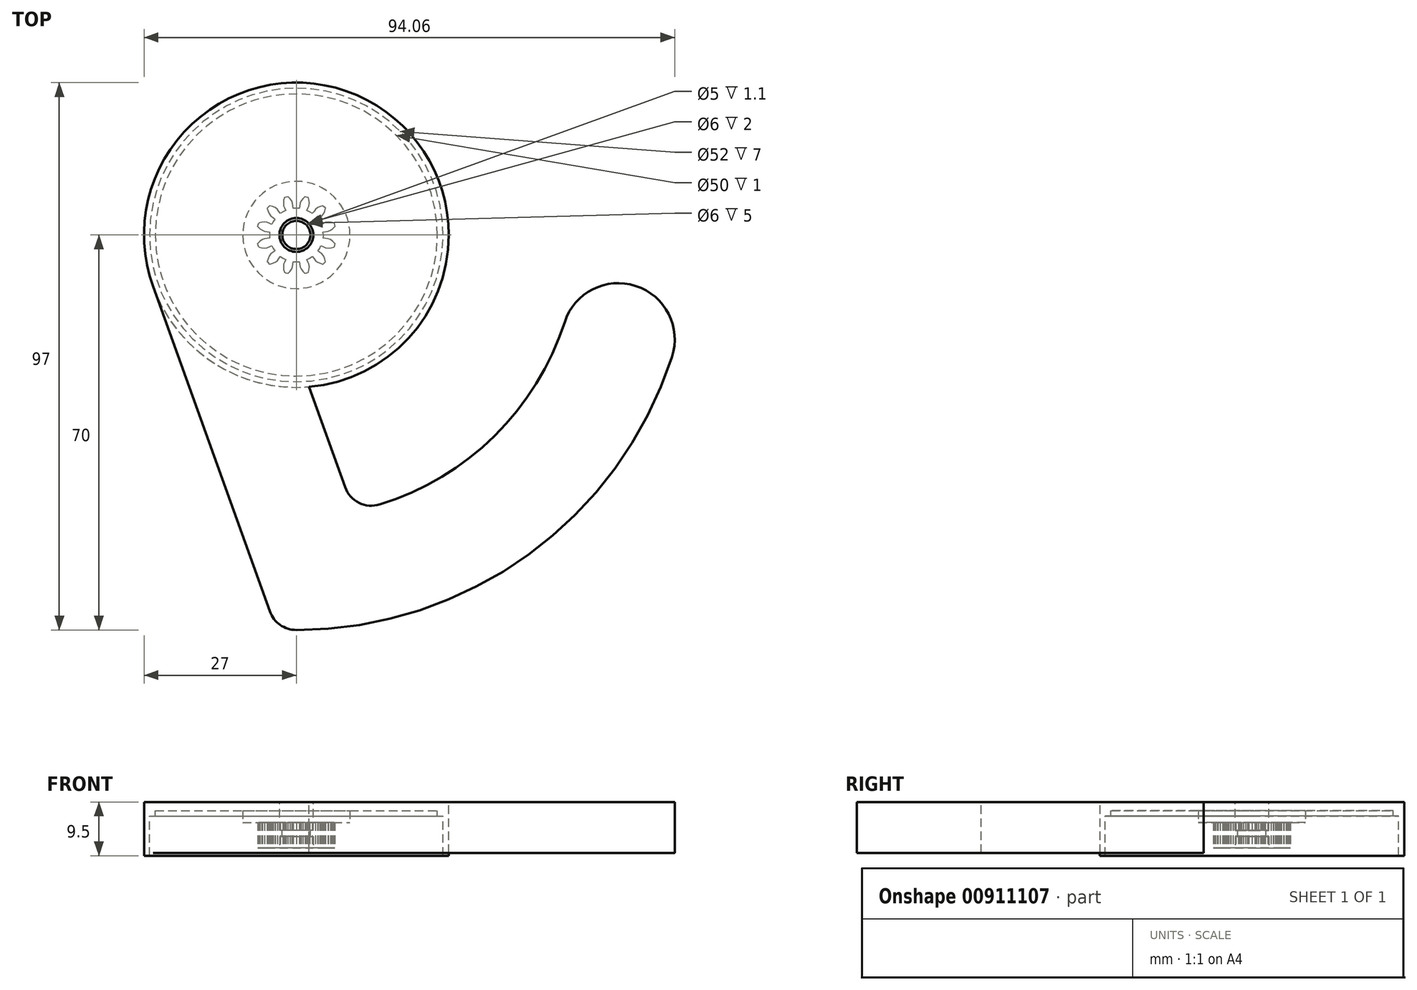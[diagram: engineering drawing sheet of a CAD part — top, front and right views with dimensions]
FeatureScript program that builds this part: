
annotation { "Feature Type Name" : "Feature", "Feature Type Description" : "" }
export const myFeature = defineFeature(function(context is Context, id is Id, definition is map)
    precondition{}
    {
        {
            var Q0;
            Q0=qCreatedBy(makeId("Top.planeOp"),FACE);
            var sketch = newSketch(context, id + "F0", { "sketchPlane" : qUnion([Q0])});
            skLineSegment(sketch, "E0", {"start": v(4.75, 0) * mm, "end": v(4.72, 0.55) * mm});
            skLineSegment(sketch, "E1", {"start": v(4.72, 0.55) * mm, "end": v(5.17, 0.6) * mm});
            skLineSegment(sketch, "E2", {"start": v(5.17, 0.6) * mm, "end": v(5.61, 0.65) * mm});
            skLineSegment(sketch, "E3", {"start": v(5.61, 0.65) * mm, "end": v(6.04, 0.84) * mm});
            skLineSegment(sketch, "E4", {"start": v(6.04, 0.84) * mm, "end": v(6.45, 1.13) * mm});
            skLineSegment(sketch, "E5", {"start": v(6.45, 1.13) * mm, "end": v(6.84, 1.51) * mm});
            skLineSegment(sketch, "E6", {"start": v(6.84, 1.51) * mm, "end": v(6.76, 1.81) * mm});
            skLineSegment(sketch, "E7", {"start": v(6.76, 1.81) * mm, "end": v(6.67, 2.1) * mm});
            skLineSegment(sketch, "E8", {"start": v(6.67, 2.1) * mm, "end": v(6.15, 2.25) * mm});
            skLineSegment(sketch, "E9", {"start": v(6.15, 2.25) * mm, "end": v(5.65, 2.3) * mm});
            skLineSegment(sketch, "E10", {"start": v(5.65, 2.3) * mm, "end": v(5.19, 2.24) * mm});
            skLineSegment(sketch, "E11", {"start": v(5.19, 2.24) * mm, "end": v(4.77, 2.06) * mm});
            skLineSegment(sketch, "E12", {"start": v(4.77, 2.06) * mm, "end": v(4.36, 1.88) * mm});
            skLineSegment(sketch, "E13", {"start": v(4.36, 1.88) * mm, "end": v(4.11, 2.38) * mm});
            skLineSegment(sketch, "E14", {"start": v(4.11, 2.38) * mm, "end": v(3.81, 2.84) * mm});
            skLineSegment(sketch, "E15", {"start": v(3.81, 2.84) * mm, "end": v(4.17, 3.1) * mm});
            skLineSegment(sketch, "E16", {"start": v(4.17, 3.1) * mm, "end": v(4.53, 3.37) * mm});
            skLineSegment(sketch, "E17", {"start": v(4.53, 3.37) * mm, "end": v(4.82, 3.74) * mm});
            skLineSegment(sketch, "E18", {"start": v(4.82, 3.74) * mm, "end": v(5.02, 4.2) * mm});
            skLineSegment(sketch, "E19", {"start": v(5.02, 4.2) * mm, "end": v(5.16, 4.73) * mm});
            skLineSegment(sketch, "E20", {"start": v(5.16, 4.73) * mm, "end": v(4.95, 4.95) * mm});
            skLineSegment(sketch, "E21", {"start": v(4.95, 4.95) * mm, "end": v(4.73, 5.16) * mm});
            skLineSegment(sketch, "E22", {"start": v(4.73, 5.16) * mm, "end": v(4.2, 5.02) * mm});
            skLineSegment(sketch, "E23", {"start": v(4.2, 5.02) * mm, "end": v(3.74, 4.82) * mm});
            skLineSegment(sketch, "E24", {"start": v(3.74, 4.82) * mm, "end": v(3.37, 4.53) * mm});
            skLineSegment(sketch, "E25", {"start": v(3.37, 4.53) * mm, "end": v(3.1, 4.17) * mm});
            skLineSegment(sketch, "E26", {"start": v(3.1, 4.17) * mm, "end": v(2.84, 3.81) * mm});
            skLineSegment(sketch, "E27", {"start": v(2.84, 3.81) * mm, "end": v(2.38, 4.11) * mm});
            skLineSegment(sketch, "E28", {"start": v(2.38, 4.11) * mm, "end": v(1.88, 4.36) * mm});
            skLineSegment(sketch, "E29", {"start": v(1.88, 4.36) * mm, "end": v(2.06, 4.77) * mm});
            skLineSegment(sketch, "E30", {"start": v(2.06, 4.77) * mm, "end": v(2.24, 5.19) * mm});
            skLineSegment(sketch, "E31", {"start": v(2.24, 5.19) * mm, "end": v(2.3, 5.65) * mm});
            skLineSegment(sketch, "E32", {"start": v(2.3, 5.65) * mm, "end": v(2.25, 6.15) * mm});
            skLineSegment(sketch, "E33", {"start": v(2.25, 6.15) * mm, "end": v(2.1, 6.67) * mm});
            skLineSegment(sketch, "E34", {"start": v(2.1, 6.67) * mm, "end": v(1.81, 6.76) * mm});
            skLineSegment(sketch, "E35", {"start": v(1.81, 6.76) * mm, "end": v(1.51, 6.84) * mm});
            skLineSegment(sketch, "E36", {"start": v(1.51, 6.84) * mm, "end": v(1.13, 6.45) * mm});
            skLineSegment(sketch, "E37", {"start": v(1.13, 6.45) * mm, "end": v(0.84, 6.04) * mm});
            skLineSegment(sketch, "E38", {"start": v(0.84, 6.04) * mm, "end": v(0.65, 5.61) * mm});
            skLineSegment(sketch, "E39", {"start": v(0.65, 5.61) * mm, "end": v(0.6, 5.17) * mm});
            skLineSegment(sketch, "E40", {"start": v(0.6, 5.17) * mm, "end": v(0.55, 4.72) * mm});
            skLineSegment(sketch, "E41", {"start": v(0.55, 4.72) * mm, "end": v(0, 4.75) * mm});
            skLineSegment(sketch, "E42", {"start": v(0, 4.75) * mm, "end": v(-0.55, 4.72) * mm});
            skLineSegment(sketch, "E43", {"start": v(-0.55, 4.72) * mm, "end": v(-0.6, 5.17) * mm});
            skLineSegment(sketch, "E44", {"start": v(-0.6, 5.17) * mm, "end": v(-0.65, 5.61) * mm});
            skLineSegment(sketch, "E45", {"start": v(-0.65, 5.61) * mm, "end": v(-0.84, 6.04) * mm});
            skLineSegment(sketch, "E46", {"start": v(-0.84, 6.04) * mm, "end": v(-1.13, 6.45) * mm});
            skLineSegment(sketch, "E47", {"start": v(-1.13, 6.45) * mm, "end": v(-1.51, 6.84) * mm});
            skLineSegment(sketch, "E48", {"start": v(-1.51, 6.84) * mm, "end": v(-1.81, 6.76) * mm});
            skLineSegment(sketch, "E49", {"start": v(-1.81, 6.76) * mm, "end": v(-2.1, 6.67) * mm});
            skLineSegment(sketch, "E50", {"start": v(-2.1, 6.67) * mm, "end": v(-2.25, 6.15) * mm});
            skLineSegment(sketch, "E51", {"start": v(-2.25, 6.15) * mm, "end": v(-2.3, 5.65) * mm});
            skLineSegment(sketch, "E52", {"start": v(-2.3, 5.65) * mm, "end": v(-2.24, 5.19) * mm});
            skLineSegment(sketch, "E53", {"start": v(-2.24, 5.19) * mm, "end": v(-2.06, 4.77) * mm});
            skLineSegment(sketch, "E54", {"start": v(-2.06, 4.77) * mm, "end": v(-1.88, 4.36) * mm});
            skLineSegment(sketch, "E55", {"start": v(-1.88, 4.36) * mm, "end": v(-2.38, 4.11) * mm});
            skLineSegment(sketch, "E56", {"start": v(-2.38, 4.11) * mm, "end": v(-2.84, 3.81) * mm});
            skLineSegment(sketch, "E57", {"start": v(-2.84, 3.81) * mm, "end": v(-3.1, 4.17) * mm});
            skLineSegment(sketch, "E58", {"start": v(-3.1, 4.17) * mm, "end": v(-3.37, 4.53) * mm});
            skLineSegment(sketch, "E59", {"start": v(-3.37, 4.53) * mm, "end": v(-3.74, 4.82) * mm});
            skLineSegment(sketch, "E60", {"start": v(-3.74, 4.82) * mm, "end": v(-4.2, 5.02) * mm});
            skLineSegment(sketch, "E61", {"start": v(-4.2, 5.02) * mm, "end": v(-4.73, 5.16) * mm});
            skLineSegment(sketch, "E62", {"start": v(-4.73, 5.16) * mm, "end": v(-4.95, 4.95) * mm});
            skLineSegment(sketch, "E63", {"start": v(-4.95, 4.95) * mm, "end": v(-5.16, 4.73) * mm});
            skLineSegment(sketch, "E64", {"start": v(-5.16, 4.73) * mm, "end": v(-5.02, 4.2) * mm});
            skLineSegment(sketch, "E65", {"start": v(-5.02, 4.2) * mm, "end": v(-4.82, 3.74) * mm});
            skLineSegment(sketch, "E66", {"start": v(-4.82, 3.74) * mm, "end": v(-4.53, 3.37) * mm});
            skLineSegment(sketch, "E67", {"start": v(-4.53, 3.37) * mm, "end": v(-4.17, 3.1) * mm});
            skLineSegment(sketch, "E68", {"start": v(-4.17, 3.1) * mm, "end": v(-3.81, 2.84) * mm});
            skLineSegment(sketch, "E69", {"start": v(-3.81, 2.84) * mm, "end": v(-4.11, 2.38) * mm});
            skLineSegment(sketch, "E70", {"start": v(-4.11, 2.38) * mm, "end": v(-4.36, 1.88) * mm});
            skLineSegment(sketch, "E71", {"start": v(-4.36, 1.88) * mm, "end": v(-4.77, 2.06) * mm});
            skLineSegment(sketch, "E72", {"start": v(-4.77, 2.06) * mm, "end": v(-5.19, 2.24) * mm});
            skLineSegment(sketch, "E73", {"start": v(-5.19, 2.24) * mm, "end": v(-5.65, 2.3) * mm});
            skLineSegment(sketch, "E74", {"start": v(-5.65, 2.3) * mm, "end": v(-6.15, 2.25) * mm});
            skLineSegment(sketch, "E75", {"start": v(-6.15, 2.25) * mm, "end": v(-6.67, 2.1) * mm});
            skLineSegment(sketch, "E76", {"start": v(-6.67, 2.1) * mm, "end": v(-6.76, 1.81) * mm});
            skLineSegment(sketch, "E77", {"start": v(-6.76, 1.81) * mm, "end": v(-6.84, 1.51) * mm});
            skLineSegment(sketch, "E78", {"start": v(-6.84, 1.51) * mm, "end": v(-6.45, 1.13) * mm});
            skLineSegment(sketch, "E79", {"start": v(-6.45, 1.13) * mm, "end": v(-6.04, 0.84) * mm});
            skLineSegment(sketch, "E80", {"start": v(-6.04, 0.84) * mm, "end": v(-5.61, 0.65) * mm});
            skLineSegment(sketch, "E81", {"start": v(-5.61, 0.65) * mm, "end": v(-5.17, 0.6) * mm});
            skLineSegment(sketch, "E82", {"start": v(-5.17, 0.6) * mm, "end": v(-4.72, 0.55) * mm});
            skLineSegment(sketch, "E83", {"start": v(-4.72, 0.55) * mm, "end": v(-4.75, 0) * mm});
            skLineSegment(sketch, "E84", {"start": v(-4.75, 0) * mm, "end": v(-4.72, -0.55) * mm});
            skLineSegment(sketch, "E85", {"start": v(-4.72, -0.55) * mm, "end": v(-5.17, -0.6) * mm});
            skLineSegment(sketch, "E86", {"start": v(-5.17, -0.6) * mm, "end": v(-5.61, -0.65) * mm});
            skLineSegment(sketch, "E87", {"start": v(-5.61, -0.65) * mm, "end": v(-6.04, -0.84) * mm});
            skLineSegment(sketch, "E88", {"start": v(-6.04, -0.84) * mm, "end": v(-6.45, -1.13) * mm});
            skLineSegment(sketch, "E89", {"start": v(-6.45, -1.13) * mm, "end": v(-6.84, -1.51) * mm});
            skLineSegment(sketch, "E90", {"start": v(-6.84, -1.51) * mm, "end": v(-6.76, -1.81) * mm});
            skLineSegment(sketch, "E91", {"start": v(-6.76, -1.81) * mm, "end": v(-6.67, -2.1) * mm});
            skLineSegment(sketch, "E92", {"start": v(-6.67, -2.1) * mm, "end": v(-6.15, -2.25) * mm});
            skLineSegment(sketch, "E93", {"start": v(-6.15, -2.25) * mm, "end": v(-5.65, -2.3) * mm});
            skLineSegment(sketch, "E94", {"start": v(-5.65, -2.3) * mm, "end": v(-5.19, -2.24) * mm});
            skLineSegment(sketch, "E95", {"start": v(-5.19, -2.24) * mm, "end": v(-4.77, -2.06) * mm});
            skLineSegment(sketch, "E96", {"start": v(-4.77, -2.06) * mm, "end": v(-4.36, -1.88) * mm});
            skLineSegment(sketch, "E97", {"start": v(-4.36, -1.88) * mm, "end": v(-4.11, -2.38) * mm});
            skLineSegment(sketch, "E98", {"start": v(-4.11, -2.38) * mm, "end": v(-3.81, -2.84) * mm});
            skLineSegment(sketch, "E99", {"start": v(-3.81, -2.84) * mm, "end": v(-4.17, -3.1) * mm});
            skLineSegment(sketch, "E100", {"start": v(-4.17, -3.1) * mm, "end": v(-4.53, -3.37) * mm});
            skLineSegment(sketch, "E101", {"start": v(-4.53, -3.37) * mm, "end": v(-4.82, -3.74) * mm});
            skLineSegment(sketch, "E102", {"start": v(-4.82, -3.74) * mm, "end": v(-5.02, -4.2) * mm});
            skLineSegment(sketch, "E103", {"start": v(-5.02, -4.2) * mm, "end": v(-5.16, -4.73) * mm});
            skLineSegment(sketch, "E104", {"start": v(-5.16, -4.73) * mm, "end": v(-4.95, -4.95) * mm});
            skLineSegment(sketch, "E105", {"start": v(-4.95, -4.95) * mm, "end": v(-4.73, -5.16) * mm});
            skLineSegment(sketch, "E106", {"start": v(-4.73, -5.16) * mm, "end": v(-4.2, -5.02) * mm});
            skLineSegment(sketch, "E107", {"start": v(-4.2, -5.02) * mm, "end": v(-3.74, -4.82) * mm});
            skLineSegment(sketch, "E108", {"start": v(-3.74, -4.82) * mm, "end": v(-3.37, -4.53) * mm});
            skLineSegment(sketch, "E109", {"start": v(-3.37, -4.53) * mm, "end": v(-3.1, -4.17) * mm});
            skLineSegment(sketch, "E110", {"start": v(-3.1, -4.17) * mm, "end": v(-2.84, -3.81) * mm});
            skLineSegment(sketch, "E111", {"start": v(-2.84, -3.81) * mm, "end": v(-2.38, -4.11) * mm});
            skLineSegment(sketch, "E112", {"start": v(-2.38, -4.11) * mm, "end": v(-1.88, -4.36) * mm});
            skLineSegment(sketch, "E113", {"start": v(-1.88, -4.36) * mm, "end": v(-2.06, -4.77) * mm});
            skLineSegment(sketch, "E114", {"start": v(-2.06, -4.77) * mm, "end": v(-2.24, -5.19) * mm});
            skLineSegment(sketch, "E115", {"start": v(-2.24, -5.19) * mm, "end": v(-2.3, -5.65) * mm});
            skLineSegment(sketch, "E116", {"start": v(-2.3, -5.65) * mm, "end": v(-2.25, -6.15) * mm});
            skLineSegment(sketch, "E117", {"start": v(-2.25, -6.15) * mm, "end": v(-2.1, -6.67) * mm});
            skLineSegment(sketch, "E118", {"start": v(-2.1, -6.67) * mm, "end": v(-1.81, -6.76) * mm});
            skLineSegment(sketch, "E119", {"start": v(-1.81, -6.76) * mm, "end": v(-1.51, -6.84) * mm});
            skLineSegment(sketch, "E120", {"start": v(-1.51, -6.84) * mm, "end": v(-1.13, -6.45) * mm});
            skLineSegment(sketch, "E121", {"start": v(-1.13, -6.45) * mm, "end": v(-0.84, -6.04) * mm});
            skLineSegment(sketch, "E122", {"start": v(-0.84, -6.04) * mm, "end": v(-0.65, -5.61) * mm});
            skLineSegment(sketch, "E123", {"start": v(-0.65, -5.61) * mm, "end": v(-0.6, -5.17) * mm});
            skLineSegment(sketch, "E124", {"start": v(-0.6, -5.17) * mm, "end": v(-0.55, -4.72) * mm});
            skLineSegment(sketch, "E125", {"start": v(-0.55, -4.72) * mm, "end": v(0, -4.75) * mm});
            skLineSegment(sketch, "E126", {"start": v(0, -4.75) * mm, "end": v(0.55, -4.72) * mm});
            skLineSegment(sketch, "E127", {"start": v(0.55, -4.72) * mm, "end": v(0.6, -5.17) * mm});
            skLineSegment(sketch, "E128", {"start": v(0.6, -5.17) * mm, "end": v(0.65, -5.61) * mm});
            skLineSegment(sketch, "E129", {"start": v(0.65, -5.61) * mm, "end": v(0.84, -6.04) * mm});
            skLineSegment(sketch, "E130", {"start": v(0.84, -6.04) * mm, "end": v(1.13, -6.45) * mm});
            skLineSegment(sketch, "E131", {"start": v(1.13, -6.45) * mm, "end": v(1.51, -6.84) * mm});
            skLineSegment(sketch, "E132", {"start": v(1.51, -6.84) * mm, "end": v(1.81, -6.76) * mm});
            skLineSegment(sketch, "E133", {"start": v(1.81, -6.76) * mm, "end": v(2.1, -6.67) * mm});
            skLineSegment(sketch, "E134", {"start": v(2.1, -6.67) * mm, "end": v(2.25, -6.15) * mm});
            skLineSegment(sketch, "E135", {"start": v(2.25, -6.15) * mm, "end": v(2.3, -5.65) * mm});
            skLineSegment(sketch, "E136", {"start": v(2.3, -5.65) * mm, "end": v(2.24, -5.19) * mm});
            skLineSegment(sketch, "E137", {"start": v(2.24, -5.19) * mm, "end": v(2.06, -4.77) * mm});
            skLineSegment(sketch, "E138", {"start": v(2.06, -4.77) * mm, "end": v(1.88, -4.36) * mm});
            skLineSegment(sketch, "E139", {"start": v(1.88, -4.36) * mm, "end": v(2.38, -4.11) * mm});
            skLineSegment(sketch, "E140", {"start": v(2.38, -4.11) * mm, "end": v(2.84, -3.81) * mm});
            skLineSegment(sketch, "E141", {"start": v(2.84, -3.81) * mm, "end": v(3.1, -4.17) * mm});
            skLineSegment(sketch, "E142", {"start": v(3.1, -4.17) * mm, "end": v(3.37, -4.53) * mm});
            skLineSegment(sketch, "E143", {"start": v(3.37, -4.53) * mm, "end": v(3.74, -4.82) * mm});
            skLineSegment(sketch, "E144", {"start": v(3.74, -4.82) * mm, "end": v(4.2, -5.02) * mm});
            skLineSegment(sketch, "E145", {"start": v(4.2, -5.02) * mm, "end": v(4.73, -5.16) * mm});
            skLineSegment(sketch, "E146", {"start": v(4.73, -5.16) * mm, "end": v(4.95, -4.95) * mm});
            skLineSegment(sketch, "E147", {"start": v(4.95, -4.95) * mm, "end": v(5.16, -4.73) * mm});
            skLineSegment(sketch, "E148", {"start": v(5.16, -4.73) * mm, "end": v(5.02, -4.2) * mm});
            skLineSegment(sketch, "E149", {"start": v(5.02, -4.2) * mm, "end": v(4.82, -3.74) * mm});
            skLineSegment(sketch, "E150", {"start": v(4.82, -3.74) * mm, "end": v(4.53, -3.37) * mm});
            skLineSegment(sketch, "E151", {"start": v(4.53, -3.37) * mm, "end": v(4.17, -3.1) * mm});
            skLineSegment(sketch, "E152", {"start": v(4.17, -3.1) * mm, "end": v(3.81, -2.84) * mm});
            skLineSegment(sketch, "E153", {"start": v(3.81, -2.84) * mm, "end": v(4.11, -2.38) * mm});
            skLineSegment(sketch, "E154", {"start": v(4.11, -2.38) * mm, "end": v(4.36, -1.88) * mm});
            skLineSegment(sketch, "E155", {"start": v(4.36, -1.88) * mm, "end": v(4.77, -2.06) * mm});
            skLineSegment(sketch, "E156", {"start": v(4.77, -2.06) * mm, "end": v(5.19, -2.24) * mm});
            skLineSegment(sketch, "E157", {"start": v(5.19, -2.24) * mm, "end": v(5.65, -2.3) * mm});
            skLineSegment(sketch, "E158", {"start": v(5.65, -2.3) * mm, "end": v(6.15, -2.25) * mm});
            skLineSegment(sketch, "E159", {"start": v(6.15, -2.25) * mm, "end": v(6.67, -2.1) * mm});
            skLineSegment(sketch, "E160", {"start": v(6.67, -2.1) * mm, "end": v(6.76, -1.81) * mm});
            skLineSegment(sketch, "E161", {"start": v(6.76, -1.81) * mm, "end": v(6.84, -1.51) * mm});
            skLineSegment(sketch, "E162", {"start": v(6.84, -1.51) * mm, "end": v(6.45, -1.13) * mm});
            skLineSegment(sketch, "E163", {"start": v(6.45, -1.13) * mm, "end": v(6.04, -0.84) * mm});
            skLineSegment(sketch, "E164", {"start": v(6.04, -0.84) * mm, "end": v(5.61, -0.65) * mm});
            skLineSegment(sketch, "E165", {"start": v(5.61, -0.65) * mm, "end": v(5.17, -0.6) * mm});
            skLineSegment(sketch, "E166", {"start": v(5.17, -0.6) * mm, "end": v(4.72, -0.55) * mm});
            skLineSegment(sketch, "E167", {"start": v(4.75, 0) * mm, "end": v(4.72, -0.55) * mm});
            skSolve(sketch);
        }
        {
            var Q0;
            Q0 = qSketchRegion(id + "F0", true);
            extrude(context, id + "F1", {"entities" : qUnion([Q0]), "depth" : 6 * mm, "offsetDistance" : 25 * mm});
        }
        {
            var Q0;
            Q0=makeQuery(id+"F1.opExtrude","CAP_FACE",FACE,{"disambiguationData":[OSD([sQuery(id+"F0.wireOp",EDGE,"E0"),sQuery(id+"F0.wireOp",EDGE,"E1"),sQuery(id+"F0.wireOp",EDGE,"E2"),sQuery(id+"F0.wireOp",EDGE,"E3"),sQuery(id+"F0.wireOp",EDGE,"E4"),sQuery(id+"F0.wireOp",EDGE,"E5"),sQuery(id+"F0.wireOp",EDGE,"E6"),sQuery(id+"F0.wireOp",EDGE,"E7"),sQuery(id+"F0.wireOp",EDGE,"E8"),sQuery(id+"F0.wireOp",EDGE,"E9"),sQuery(id+"F0.wireOp",EDGE,"E10"),sQuery(id+"F0.wireOp",EDGE,"E11"),sQuery(id+"F0.wireOp",EDGE,"E12"),sQuery(id+"F0.wireOp",EDGE,"E13"),sQuery(id+"F0.wireOp",EDGE,"E14"),sQuery(id+"F0.wireOp",EDGE,"E15"),sQuery(id+"F0.wireOp",EDGE,"E16"),sQuery(id+"F0.wireOp",EDGE,"E17"),sQuery(id+"F0.wireOp",EDGE,"E18"),sQuery(id+"F0.wireOp",EDGE,"E19"),sQuery(id+"F0.wireOp",EDGE,"E20"),sQuery(id+"F0.wireOp",EDGE,"E21"),sQuery(id+"F0.wireOp",EDGE,"E22"),sQuery(id+"F0.wireOp",EDGE,"E23"),sQuery(id+"F0.wireOp",EDGE,"E24"),sQuery(id+"F0.wireOp",EDGE,"E25"),sQuery(id+"F0.wireOp",EDGE,"E26"),sQuery(id+"F0.wireOp",EDGE,"E27"),sQuery(id+"F0.wireOp",EDGE,"E28"),sQuery(id+"F0.wireOp",EDGE,"E29"),sQuery(id+"F0.wireOp",EDGE,"E30"),sQuery(id+"F0.wireOp",EDGE,"E31"),sQuery(id+"F0.wireOp",EDGE,"E32"),sQuery(id+"F0.wireOp",EDGE,"E33"),sQuery(id+"F0.wireOp",EDGE,"E34"),sQuery(id+"F0.wireOp",EDGE,"E35"),sQuery(id+"F0.wireOp",EDGE,"E36"),sQuery(id+"F0.wireOp",EDGE,"E37"),sQuery(id+"F0.wireOp",EDGE,"E38"),sQuery(id+"F0.wireOp",EDGE,"E39"),sQuery(id+"F0.wireOp",EDGE,"E40"),sQuery(id+"F0.wireOp",EDGE,"E41"),sQuery(id+"F0.wireOp",EDGE,"E42"),sQuery(id+"F0.wireOp",EDGE,"E43"),sQuery(id+"F0.wireOp",EDGE,"E44"),sQuery(id+"F0.wireOp",EDGE,"E45"),sQuery(id+"F0.wireOp",EDGE,"E46"),sQuery(id+"F0.wireOp",EDGE,"E47"),sQuery(id+"F0.wireOp",EDGE,"E48"),sQuery(id+"F0.wireOp",EDGE,"E49"),sQuery(id+"F0.wireOp",EDGE,"E50"),sQuery(id+"F0.wireOp",EDGE,"E51"),sQuery(id+"F0.wireOp",EDGE,"E52"),sQuery(id+"F0.wireOp",EDGE,"E53"),sQuery(id+"F0.wireOp",EDGE,"E54"),sQuery(id+"F0.wireOp",EDGE,"E55"),sQuery(id+"F0.wireOp",EDGE,"E56"),sQuery(id+"F0.wireOp",EDGE,"E57"),sQuery(id+"F0.wireOp",EDGE,"E58"),sQuery(id+"F0.wireOp",EDGE,"E59"),sQuery(id+"F0.wireOp",EDGE,"E60"),sQuery(id+"F0.wireOp",EDGE,"E61"),sQuery(id+"F0.wireOp",EDGE,"E62"),sQuery(id+"F0.wireOp",EDGE,"E63"),sQuery(id+"F0.wireOp",EDGE,"E64"),sQuery(id+"F0.wireOp",EDGE,"E65"),sQuery(id+"F0.wireOp",EDGE,"E66"),sQuery(id+"F0.wireOp",EDGE,"E67"),sQuery(id+"F0.wireOp",EDGE,"E68"),sQuery(id+"F0.wireOp",EDGE,"E69"),sQuery(id+"F0.wireOp",EDGE,"E70"),sQuery(id+"F0.wireOp",EDGE,"E71"),sQuery(id+"F0.wireOp",EDGE,"E72"),sQuery(id+"F0.wireOp",EDGE,"E73"),sQuery(id+"F0.wireOp",EDGE,"E74"),sQuery(id+"F0.wireOp",EDGE,"E75"),sQuery(id+"F0.wireOp",EDGE,"E76"),sQuery(id+"F0.wireOp",EDGE,"E77"),sQuery(id+"F0.wireOp",EDGE,"E78"),sQuery(id+"F0.wireOp",EDGE,"E79"),sQuery(id+"F0.wireOp",EDGE,"E80"),sQuery(id+"F0.wireOp",EDGE,"E81"),sQuery(id+"F0.wireOp",EDGE,"E82"),sQuery(id+"F0.wireOp",EDGE,"E83"),sQuery(id+"F0.wireOp",EDGE,"E84"),sQuery(id+"F0.wireOp",EDGE,"E85"),sQuery(id+"F0.wireOp",EDGE,"E86"),sQuery(id+"F0.wireOp",EDGE,"E87"),sQuery(id+"F0.wireOp",EDGE,"E88"),sQuery(id+"F0.wireOp",EDGE,"E89"),sQuery(id+"F0.wireOp",EDGE,"E90"),sQuery(id+"F0.wireOp",EDGE,"E91"),sQuery(id+"F0.wireOp",EDGE,"E92"),sQuery(id+"F0.wireOp",EDGE,"E93"),sQuery(id+"F0.wireOp",EDGE,"E94"),sQuery(id+"F0.wireOp",EDGE,"E95"),sQuery(id+"F0.wireOp",EDGE,"E96"),sQuery(id+"F0.wireOp",EDGE,"E97"),sQuery(id+"F0.wireOp",EDGE,"E98"),sQuery(id+"F0.wireOp",EDGE,"E99"),sQuery(id+"F0.wireOp",EDGE,"E100"),sQuery(id+"F0.wireOp",EDGE,"E101"),sQuery(id+"F0.wireOp",EDGE,"E102"),sQuery(id+"F0.wireOp",EDGE,"E103"),sQuery(id+"F0.wireOp",EDGE,"E104"),sQuery(id+"F0.wireOp",EDGE,"E105"),sQuery(id+"F0.wireOp",EDGE,"E106"),sQuery(id+"F0.wireOp",EDGE,"E107"),sQuery(id+"F0.wireOp",EDGE,"E108"),sQuery(id+"F0.wireOp",EDGE,"E109"),sQuery(id+"F0.wireOp",EDGE,"E110"),sQuery(id+"F0.wireOp",EDGE,"E111"),sQuery(id+"F0.wireOp",EDGE,"E112"),sQuery(id+"F0.wireOp",EDGE,"E113"),sQuery(id+"F0.wireOp",EDGE,"E114"),sQuery(id+"F0.wireOp",EDGE,"E115"),sQuery(id+"F0.wireOp",EDGE,"E116"),sQuery(id+"F0.wireOp",EDGE,"E117"),sQuery(id+"F0.wireOp",EDGE,"E118"),sQuery(id+"F0.wireOp",EDGE,"E119"),sQuery(id+"F0.wireOp",EDGE,"E120"),sQuery(id+"F0.wireOp",EDGE,"E121"),sQuery(id+"F0.wireOp",EDGE,"E122"),sQuery(id+"F0.wireOp",EDGE,"E123"),sQuery(id+"F0.wireOp",EDGE,"E124"),sQuery(id+"F0.wireOp",EDGE,"E125"),sQuery(id+"F0.wireOp",EDGE,"E126"),sQuery(id+"F0.wireOp",EDGE,"E127"),sQuery(id+"F0.wireOp",EDGE,"E128"),sQuery(id+"F0.wireOp",EDGE,"E129"),sQuery(id+"F0.wireOp",EDGE,"E130"),sQuery(id+"F0.wireOp",EDGE,"E131"),sQuery(id+"F0.wireOp",EDGE,"E132"),sQuery(id+"F0.wireOp",EDGE,"E133"),sQuery(id+"F0.wireOp",EDGE,"E134"),sQuery(id+"F0.wireOp",EDGE,"E135"),sQuery(id+"F0.wireOp",EDGE,"E136"),sQuery(id+"F0.wireOp",EDGE,"E137"),sQuery(id+"F0.wireOp",EDGE,"E138"),sQuery(id+"F0.wireOp",EDGE,"E139"),sQuery(id+"F0.wireOp",EDGE,"E140"),sQuery(id+"F0.wireOp",EDGE,"E141"),sQuery(id+"F0.wireOp",EDGE,"E142"),sQuery(id+"F0.wireOp",EDGE,"E143"),sQuery(id+"F0.wireOp",EDGE,"E144"),sQuery(id+"F0.wireOp",EDGE,"E145"),sQuery(id+"F0.wireOp",EDGE,"E146"),sQuery(id+"F0.wireOp",EDGE,"E147"),sQuery(id+"F0.wireOp",EDGE,"E148"),sQuery(id+"F0.wireOp",EDGE,"E149"),sQuery(id+"F0.wireOp",EDGE,"E150"),sQuery(id+"F0.wireOp",EDGE,"E151"),sQuery(id+"F0.wireOp",EDGE,"E152"),sQuery(id+"F0.wireOp",EDGE,"E153"),sQuery(id+"F0.wireOp",EDGE,"E154"),sQuery(id+"F0.wireOp",EDGE,"E155"),sQuery(id+"F0.wireOp",EDGE,"E156"),sQuery(id+"F0.wireOp",EDGE,"E157"),sQuery(id+"F0.wireOp",EDGE,"E158"),sQuery(id+"F0.wireOp",EDGE,"E159"),sQuery(id+"F0.wireOp",EDGE,"E160"),sQuery(id+"F0.wireOp",EDGE,"E161"),sQuery(id+"F0.wireOp",EDGE,"E162"),sQuery(id+"F0.wireOp",EDGE,"E163"),sQuery(id+"F0.wireOp",EDGE,"E164"),sQuery(id+"F0.wireOp",EDGE,"E165"),sQuery(id+"F0.wireOp",EDGE,"E166"),sQuery(id+"F0.wireOp",EDGE,"E167")])],"isStart":true});
            var sketch = newSketch(context, id + "F2", { "sketchPlane" : qUnion([Q0])});
            skCircle(sketch, "E168", {"center": v(0, 0) * mm, "radius": 3 * mm});
            skSolve(sketch);
        }
        {
            var Q0;
            Q0 = qSketchRegion(id + "F2", true);
            extrude(context, id + "F3", {"entities" : qUnion([Q0]), "operationType" : NewBodyOperationType.REMOVE, "oppositeDirection" : true, "depth" : 2 * mm, "offsetDistance" : 25 * mm});
        }
        {
            var Q0;
            Q0=makeQuery(id+"F1.opExtrude","CAP_FACE",FACE,{"disambiguationData":[OSD([sQuery(id+"F0.wireOp",EDGE,"E0"),sQuery(id+"F0.wireOp",EDGE,"E1"),sQuery(id+"F0.wireOp",EDGE,"E2"),sQuery(id+"F0.wireOp",EDGE,"E3"),sQuery(id+"F0.wireOp",EDGE,"E4"),sQuery(id+"F0.wireOp",EDGE,"E5"),sQuery(id+"F0.wireOp",EDGE,"E6"),sQuery(id+"F0.wireOp",EDGE,"E7"),sQuery(id+"F0.wireOp",EDGE,"E8"),sQuery(id+"F0.wireOp",EDGE,"E9"),sQuery(id+"F0.wireOp",EDGE,"E10"),sQuery(id+"F0.wireOp",EDGE,"E11"),sQuery(id+"F0.wireOp",EDGE,"E12"),sQuery(id+"F0.wireOp",EDGE,"E13"),sQuery(id+"F0.wireOp",EDGE,"E14"),sQuery(id+"F0.wireOp",EDGE,"E15"),sQuery(id+"F0.wireOp",EDGE,"E16"),sQuery(id+"F0.wireOp",EDGE,"E17"),sQuery(id+"F0.wireOp",EDGE,"E18"),sQuery(id+"F0.wireOp",EDGE,"E19"),sQuery(id+"F0.wireOp",EDGE,"E20"),sQuery(id+"F0.wireOp",EDGE,"E21"),sQuery(id+"F0.wireOp",EDGE,"E22"),sQuery(id+"F0.wireOp",EDGE,"E23"),sQuery(id+"F0.wireOp",EDGE,"E24"),sQuery(id+"F0.wireOp",EDGE,"E25"),sQuery(id+"F0.wireOp",EDGE,"E26"),sQuery(id+"F0.wireOp",EDGE,"E27"),sQuery(id+"F0.wireOp",EDGE,"E28"),sQuery(id+"F0.wireOp",EDGE,"E29"),sQuery(id+"F0.wireOp",EDGE,"E30"),sQuery(id+"F0.wireOp",EDGE,"E31"),sQuery(id+"F0.wireOp",EDGE,"E32"),sQuery(id+"F0.wireOp",EDGE,"E33"),sQuery(id+"F0.wireOp",EDGE,"E34"),sQuery(id+"F0.wireOp",EDGE,"E35"),sQuery(id+"F0.wireOp",EDGE,"E36"),sQuery(id+"F0.wireOp",EDGE,"E37"),sQuery(id+"F0.wireOp",EDGE,"E38"),sQuery(id+"F0.wireOp",EDGE,"E39"),sQuery(id+"F0.wireOp",EDGE,"E40"),sQuery(id+"F0.wireOp",EDGE,"E41"),sQuery(id+"F0.wireOp",EDGE,"E42"),sQuery(id+"F0.wireOp",EDGE,"E43"),sQuery(id+"F0.wireOp",EDGE,"E44"),sQuery(id+"F0.wireOp",EDGE,"E45"),sQuery(id+"F0.wireOp",EDGE,"E46"),sQuery(id+"F0.wireOp",EDGE,"E47"),sQuery(id+"F0.wireOp",EDGE,"E48"),sQuery(id+"F0.wireOp",EDGE,"E49"),sQuery(id+"F0.wireOp",EDGE,"E50"),sQuery(id+"F0.wireOp",EDGE,"E51"),sQuery(id+"F0.wireOp",EDGE,"E52"),sQuery(id+"F0.wireOp",EDGE,"E53"),sQuery(id+"F0.wireOp",EDGE,"E54"),sQuery(id+"F0.wireOp",EDGE,"E55"),sQuery(id+"F0.wireOp",EDGE,"E56"),sQuery(id+"F0.wireOp",EDGE,"E57"),sQuery(id+"F0.wireOp",EDGE,"E58"),sQuery(id+"F0.wireOp",EDGE,"E59"),sQuery(id+"F0.wireOp",EDGE,"E60"),sQuery(id+"F0.wireOp",EDGE,"E61"),sQuery(id+"F0.wireOp",EDGE,"E62"),sQuery(id+"F0.wireOp",EDGE,"E63"),sQuery(id+"F0.wireOp",EDGE,"E64"),sQuery(id+"F0.wireOp",EDGE,"E65"),sQuery(id+"F0.wireOp",EDGE,"E66"),sQuery(id+"F0.wireOp",EDGE,"E67"),sQuery(id+"F0.wireOp",EDGE,"E68"),sQuery(id+"F0.wireOp",EDGE,"E69"),sQuery(id+"F0.wireOp",EDGE,"E70"),sQuery(id+"F0.wireOp",EDGE,"E71"),sQuery(id+"F0.wireOp",EDGE,"E72"),sQuery(id+"F0.wireOp",EDGE,"E73"),sQuery(id+"F0.wireOp",EDGE,"E74"),sQuery(id+"F0.wireOp",EDGE,"E75"),sQuery(id+"F0.wireOp",EDGE,"E76"),sQuery(id+"F0.wireOp",EDGE,"E77"),sQuery(id+"F0.wireOp",EDGE,"E78"),sQuery(id+"F0.wireOp",EDGE,"E79"),sQuery(id+"F0.wireOp",EDGE,"E80"),sQuery(id+"F0.wireOp",EDGE,"E81"),sQuery(id+"F0.wireOp",EDGE,"E82"),sQuery(id+"F0.wireOp",EDGE,"E83"),sQuery(id+"F0.wireOp",EDGE,"E84"),sQuery(id+"F0.wireOp",EDGE,"E85"),sQuery(id+"F0.wireOp",EDGE,"E86"),sQuery(id+"F0.wireOp",EDGE,"E87"),sQuery(id+"F0.wireOp",EDGE,"E88"),sQuery(id+"F0.wireOp",EDGE,"E89"),sQuery(id+"F0.wireOp",EDGE,"E90"),sQuery(id+"F0.wireOp",EDGE,"E91"),sQuery(id+"F0.wireOp",EDGE,"E92"),sQuery(id+"F0.wireOp",EDGE,"E93"),sQuery(id+"F0.wireOp",EDGE,"E94"),sQuery(id+"F0.wireOp",EDGE,"E95"),sQuery(id+"F0.wireOp",EDGE,"E96"),sQuery(id+"F0.wireOp",EDGE,"E97"),sQuery(id+"F0.wireOp",EDGE,"E98"),sQuery(id+"F0.wireOp",EDGE,"E99"),sQuery(id+"F0.wireOp",EDGE,"E100"),sQuery(id+"F0.wireOp",EDGE,"E101"),sQuery(id+"F0.wireOp",EDGE,"E102"),sQuery(id+"F0.wireOp",EDGE,"E103"),sQuery(id+"F0.wireOp",EDGE,"E104"),sQuery(id+"F0.wireOp",EDGE,"E105"),sQuery(id+"F0.wireOp",EDGE,"E106"),sQuery(id+"F0.wireOp",EDGE,"E107"),sQuery(id+"F0.wireOp",EDGE,"E108"),sQuery(id+"F0.wireOp",EDGE,"E109"),sQuery(id+"F0.wireOp",EDGE,"E110"),sQuery(id+"F0.wireOp",EDGE,"E111"),sQuery(id+"F0.wireOp",EDGE,"E112"),sQuery(id+"F0.wireOp",EDGE,"E113"),sQuery(id+"F0.wireOp",EDGE,"E114"),sQuery(id+"F0.wireOp",EDGE,"E115"),sQuery(id+"F0.wireOp",EDGE,"E116"),sQuery(id+"F0.wireOp",EDGE,"E117"),sQuery(id+"F0.wireOp",EDGE,"E118"),sQuery(id+"F0.wireOp",EDGE,"E119"),sQuery(id+"F0.wireOp",EDGE,"E120"),sQuery(id+"F0.wireOp",EDGE,"E121"),sQuery(id+"F0.wireOp",EDGE,"E122"),sQuery(id+"F0.wireOp",EDGE,"E123"),sQuery(id+"F0.wireOp",EDGE,"E124"),sQuery(id+"F0.wireOp",EDGE,"E125"),sQuery(id+"F0.wireOp",EDGE,"E126"),sQuery(id+"F0.wireOp",EDGE,"E127"),sQuery(id+"F0.wireOp",EDGE,"E128"),sQuery(id+"F0.wireOp",EDGE,"E129"),sQuery(id+"F0.wireOp",EDGE,"E130"),sQuery(id+"F0.wireOp",EDGE,"E131"),sQuery(id+"F0.wireOp",EDGE,"E132"),sQuery(id+"F0.wireOp",EDGE,"E133"),sQuery(id+"F0.wireOp",EDGE,"E134"),sQuery(id+"F0.wireOp",EDGE,"E135"),sQuery(id+"F0.wireOp",EDGE,"E136"),sQuery(id+"F0.wireOp",EDGE,"E137"),sQuery(id+"F0.wireOp",EDGE,"E138"),sQuery(id+"F0.wireOp",EDGE,"E139"),sQuery(id+"F0.wireOp",EDGE,"E140"),sQuery(id+"F0.wireOp",EDGE,"E141"),sQuery(id+"F0.wireOp",EDGE,"E142"),sQuery(id+"F0.wireOp",EDGE,"E143"),sQuery(id+"F0.wireOp",EDGE,"E144"),sQuery(id+"F0.wireOp",EDGE,"E145"),sQuery(id+"F0.wireOp",EDGE,"E146"),sQuery(id+"F0.wireOp",EDGE,"E147"),sQuery(id+"F0.wireOp",EDGE,"E148"),sQuery(id+"F0.wireOp",EDGE,"E149"),sQuery(id+"F0.wireOp",EDGE,"E150"),sQuery(id+"F0.wireOp",EDGE,"E151"),sQuery(id+"F0.wireOp",EDGE,"E152"),sQuery(id+"F0.wireOp",EDGE,"E153"),sQuery(id+"F0.wireOp",EDGE,"E154"),sQuery(id+"F0.wireOp",EDGE,"E155"),sQuery(id+"F0.wireOp",EDGE,"E156"),sQuery(id+"F0.wireOp",EDGE,"E157"),sQuery(id+"F0.wireOp",EDGE,"E158"),sQuery(id+"F0.wireOp",EDGE,"E159"),sQuery(id+"F0.wireOp",EDGE,"E160"),sQuery(id+"F0.wireOp",EDGE,"E161"),sQuery(id+"F0.wireOp",EDGE,"E162"),sQuery(id+"F0.wireOp",EDGE,"E163"),sQuery(id+"F0.wireOp",EDGE,"E164"),sQuery(id+"F0.wireOp",EDGE,"E165"),sQuery(id+"F0.wireOp",EDGE,"E166"),sQuery(id+"F0.wireOp",EDGE,"E167")])],"isStart":false});
            var sketch = newSketch(context, id + "F4", { "sketchPlane" : qUnion([Q0])});
            skCircle(sketch, "E169", {"center": v(0, 0) * mm, "radius": 2.5 * mm});
            skSolve(sketch);
        }
        {
            var Q0;
            Q0 = qSketchRegion(id + "F4", true);
            extrude(context, id + "F5", {"entities" : qUnion([Q0]), "operationType" : NewBodyOperationType.REMOVE, "oppositeDirection" : true, "depth" : 25 * mm, "offsetDistance" : 25 * mm});
        }
        {
            var Q0;
            Q0=makeQuery(id+"F1.opExtrude","CAP_FACE",FACE,{"disambiguationData":[OSD([sQuery(id+"F0.wireOp",EDGE,"E0"),sQuery(id+"F0.wireOp",EDGE,"E1"),sQuery(id+"F0.wireOp",EDGE,"E2"),sQuery(id+"F0.wireOp",EDGE,"E3"),sQuery(id+"F0.wireOp",EDGE,"E4"),sQuery(id+"F0.wireOp",EDGE,"E5"),sQuery(id+"F0.wireOp",EDGE,"E6"),sQuery(id+"F0.wireOp",EDGE,"E7"),sQuery(id+"F0.wireOp",EDGE,"E8"),sQuery(id+"F0.wireOp",EDGE,"E9"),sQuery(id+"F0.wireOp",EDGE,"E10"),sQuery(id+"F0.wireOp",EDGE,"E11"),sQuery(id+"F0.wireOp",EDGE,"E12"),sQuery(id+"F0.wireOp",EDGE,"E13"),sQuery(id+"F0.wireOp",EDGE,"E14"),sQuery(id+"F0.wireOp",EDGE,"E15"),sQuery(id+"F0.wireOp",EDGE,"E16"),sQuery(id+"F0.wireOp",EDGE,"E17"),sQuery(id+"F0.wireOp",EDGE,"E18"),sQuery(id+"F0.wireOp",EDGE,"E19"),sQuery(id+"F0.wireOp",EDGE,"E20"),sQuery(id+"F0.wireOp",EDGE,"E21"),sQuery(id+"F0.wireOp",EDGE,"E22"),sQuery(id+"F0.wireOp",EDGE,"E23"),sQuery(id+"F0.wireOp",EDGE,"E24"),sQuery(id+"F0.wireOp",EDGE,"E25"),sQuery(id+"F0.wireOp",EDGE,"E26"),sQuery(id+"F0.wireOp",EDGE,"E27"),sQuery(id+"F0.wireOp",EDGE,"E28"),sQuery(id+"F0.wireOp",EDGE,"E29"),sQuery(id+"F0.wireOp",EDGE,"E30"),sQuery(id+"F0.wireOp",EDGE,"E31"),sQuery(id+"F0.wireOp",EDGE,"E32"),sQuery(id+"F0.wireOp",EDGE,"E33"),sQuery(id+"F0.wireOp",EDGE,"E34"),sQuery(id+"F0.wireOp",EDGE,"E35"),sQuery(id+"F0.wireOp",EDGE,"E36"),sQuery(id+"F0.wireOp",EDGE,"E37"),sQuery(id+"F0.wireOp",EDGE,"E38"),sQuery(id+"F0.wireOp",EDGE,"E39"),sQuery(id+"F0.wireOp",EDGE,"E40"),sQuery(id+"F0.wireOp",EDGE,"E41"),sQuery(id+"F0.wireOp",EDGE,"E42"),sQuery(id+"F0.wireOp",EDGE,"E43"),sQuery(id+"F0.wireOp",EDGE,"E44"),sQuery(id+"F0.wireOp",EDGE,"E45"),sQuery(id+"F0.wireOp",EDGE,"E46"),sQuery(id+"F0.wireOp",EDGE,"E47"),sQuery(id+"F0.wireOp",EDGE,"E48"),sQuery(id+"F0.wireOp",EDGE,"E49"),sQuery(id+"F0.wireOp",EDGE,"E50"),sQuery(id+"F0.wireOp",EDGE,"E51"),sQuery(id+"F0.wireOp",EDGE,"E52"),sQuery(id+"F0.wireOp",EDGE,"E53"),sQuery(id+"F0.wireOp",EDGE,"E54"),sQuery(id+"F0.wireOp",EDGE,"E55"),sQuery(id+"F0.wireOp",EDGE,"E56"),sQuery(id+"F0.wireOp",EDGE,"E57"),sQuery(id+"F0.wireOp",EDGE,"E58"),sQuery(id+"F0.wireOp",EDGE,"E59"),sQuery(id+"F0.wireOp",EDGE,"E60"),sQuery(id+"F0.wireOp",EDGE,"E61"),sQuery(id+"F0.wireOp",EDGE,"E62"),sQuery(id+"F0.wireOp",EDGE,"E63"),sQuery(id+"F0.wireOp",EDGE,"E64"),sQuery(id+"F0.wireOp",EDGE,"E65"),sQuery(id+"F0.wireOp",EDGE,"E66"),sQuery(id+"F0.wireOp",EDGE,"E67"),sQuery(id+"F0.wireOp",EDGE,"E68"),sQuery(id+"F0.wireOp",EDGE,"E69"),sQuery(id+"F0.wireOp",EDGE,"E70"),sQuery(id+"F0.wireOp",EDGE,"E71"),sQuery(id+"F0.wireOp",EDGE,"E72"),sQuery(id+"F0.wireOp",EDGE,"E73"),sQuery(id+"F0.wireOp",EDGE,"E74"),sQuery(id+"F0.wireOp",EDGE,"E75"),sQuery(id+"F0.wireOp",EDGE,"E76"),sQuery(id+"F0.wireOp",EDGE,"E77"),sQuery(id+"F0.wireOp",EDGE,"E78"),sQuery(id+"F0.wireOp",EDGE,"E79"),sQuery(id+"F0.wireOp",EDGE,"E80"),sQuery(id+"F0.wireOp",EDGE,"E81"),sQuery(id+"F0.wireOp",EDGE,"E82"),sQuery(id+"F0.wireOp",EDGE,"E83"),sQuery(id+"F0.wireOp",EDGE,"E84"),sQuery(id+"F0.wireOp",EDGE,"E85"),sQuery(id+"F0.wireOp",EDGE,"E86"),sQuery(id+"F0.wireOp",EDGE,"E87"),sQuery(id+"F0.wireOp",EDGE,"E88"),sQuery(id+"F0.wireOp",EDGE,"E89"),sQuery(id+"F0.wireOp",EDGE,"E90"),sQuery(id+"F0.wireOp",EDGE,"E91"),sQuery(id+"F0.wireOp",EDGE,"E92"),sQuery(id+"F0.wireOp",EDGE,"E93"),sQuery(id+"F0.wireOp",EDGE,"E94"),sQuery(id+"F0.wireOp",EDGE,"E95"),sQuery(id+"F0.wireOp",EDGE,"E96"),sQuery(id+"F0.wireOp",EDGE,"E97"),sQuery(id+"F0.wireOp",EDGE,"E98"),sQuery(id+"F0.wireOp",EDGE,"E99"),sQuery(id+"F0.wireOp",EDGE,"E100"),sQuery(id+"F0.wireOp",EDGE,"E101"),sQuery(id+"F0.wireOp",EDGE,"E102"),sQuery(id+"F0.wireOp",EDGE,"E103"),sQuery(id+"F0.wireOp",EDGE,"E104"),sQuery(id+"F0.wireOp",EDGE,"E105"),sQuery(id+"F0.wireOp",EDGE,"E106"),sQuery(id+"F0.wireOp",EDGE,"E107"),sQuery(id+"F0.wireOp",EDGE,"E108"),sQuery(id+"F0.wireOp",EDGE,"E109"),sQuery(id+"F0.wireOp",EDGE,"E110"),sQuery(id+"F0.wireOp",EDGE,"E111"),sQuery(id+"F0.wireOp",EDGE,"E112"),sQuery(id+"F0.wireOp",EDGE,"E113"),sQuery(id+"F0.wireOp",EDGE,"E114"),sQuery(id+"F0.wireOp",EDGE,"E115"),sQuery(id+"F0.wireOp",EDGE,"E116"),sQuery(id+"F0.wireOp",EDGE,"E117"),sQuery(id+"F0.wireOp",EDGE,"E118"),sQuery(id+"F0.wireOp",EDGE,"E119"),sQuery(id+"F0.wireOp",EDGE,"E120"),sQuery(id+"F0.wireOp",EDGE,"E121"),sQuery(id+"F0.wireOp",EDGE,"E122"),sQuery(id+"F0.wireOp",EDGE,"E123"),sQuery(id+"F0.wireOp",EDGE,"E124"),sQuery(id+"F0.wireOp",EDGE,"E125"),sQuery(id+"F0.wireOp",EDGE,"E126"),sQuery(id+"F0.wireOp",EDGE,"E127"),sQuery(id+"F0.wireOp",EDGE,"E128"),sQuery(id+"F0.wireOp",EDGE,"E129"),sQuery(id+"F0.wireOp",EDGE,"E130"),sQuery(id+"F0.wireOp",EDGE,"E131"),sQuery(id+"F0.wireOp",EDGE,"E132"),sQuery(id+"F0.wireOp",EDGE,"E133"),sQuery(id+"F0.wireOp",EDGE,"E134"),sQuery(id+"F0.wireOp",EDGE,"E135"),sQuery(id+"F0.wireOp",EDGE,"E136"),sQuery(id+"F0.wireOp",EDGE,"E137"),sQuery(id+"F0.wireOp",EDGE,"E138"),sQuery(id+"F0.wireOp",EDGE,"E139"),sQuery(id+"F0.wireOp",EDGE,"E140"),sQuery(id+"F0.wireOp",EDGE,"E141"),sQuery(id+"F0.wireOp",EDGE,"E142"),sQuery(id+"F0.wireOp",EDGE,"E143"),sQuery(id+"F0.wireOp",EDGE,"E144"),sQuery(id+"F0.wireOp",EDGE,"E145"),sQuery(id+"F0.wireOp",EDGE,"E146"),sQuery(id+"F0.wireOp",EDGE,"E147"),sQuery(id+"F0.wireOp",EDGE,"E148"),sQuery(id+"F0.wireOp",EDGE,"E149"),sQuery(id+"F0.wireOp",EDGE,"E150"),sQuery(id+"F0.wireOp",EDGE,"E151"),sQuery(id+"F0.wireOp",EDGE,"E152"),sQuery(id+"F0.wireOp",EDGE,"E153"),sQuery(id+"F0.wireOp",EDGE,"E154"),sQuery(id+"F0.wireOp",EDGE,"E155"),sQuery(id+"F0.wireOp",EDGE,"E156"),sQuery(id+"F0.wireOp",EDGE,"E157"),sQuery(id+"F0.wireOp",EDGE,"E158"),sQuery(id+"F0.wireOp",EDGE,"E159"),sQuery(id+"F0.wireOp",EDGE,"E160"),sQuery(id+"F0.wireOp",EDGE,"E161"),sQuery(id+"F0.wireOp",EDGE,"E162"),sQuery(id+"F0.wireOp",EDGE,"E163"),sQuery(id+"F0.wireOp",EDGE,"E164"),sQuery(id+"F0.wireOp",EDGE,"E165"),sQuery(id+"F0.wireOp",EDGE,"E166"),sQuery(id+"F0.wireOp",EDGE,"E167")])],"isStart":false});
            extrude(context, id + "F6", {"entities" : qUnion([Q0]), "operationType" : NewBodyOperationType.REMOVE, "oppositeDirection" : true, "depth" : 1.5 * mm, "offsetDistance" : 25 * mm});
        }
        {
            var Q0;
            Q0=makeQuery(id+"F6.boolean.opBoolean","COPY",FACE,{"derivedFrom":makeQuery(id+"F6.opExtrude","CAP_FACE",FACE,{"disambiguationData":[OSD([sQuery(id+"F0.wireOp",EDGE,"E0"),sQuery(id+"F0.wireOp",EDGE,"E1"),sQuery(id+"F0.wireOp",EDGE,"E2"),sQuery(id+"F0.wireOp",EDGE,"E3"),sQuery(id+"F0.wireOp",EDGE,"E4"),sQuery(id+"F0.wireOp",EDGE,"E5"),sQuery(id+"F0.wireOp",EDGE,"E6"),sQuery(id+"F0.wireOp",EDGE,"E7"),sQuery(id+"F0.wireOp",EDGE,"E8"),sQuery(id+"F0.wireOp",EDGE,"E9"),sQuery(id+"F0.wireOp",EDGE,"E10"),sQuery(id+"F0.wireOp",EDGE,"E11"),sQuery(id+"F0.wireOp",EDGE,"E12"),sQuery(id+"F0.wireOp",EDGE,"E13"),sQuery(id+"F0.wireOp",EDGE,"E14"),sQuery(id+"F0.wireOp",EDGE,"E15"),sQuery(id+"F0.wireOp",EDGE,"E16"),sQuery(id+"F0.wireOp",EDGE,"E17"),sQuery(id+"F0.wireOp",EDGE,"E18"),sQuery(id+"F0.wireOp",EDGE,"E19"),sQuery(id+"F0.wireOp",EDGE,"E20"),sQuery(id+"F0.wireOp",EDGE,"E21"),sQuery(id+"F0.wireOp",EDGE,"E22"),sQuery(id+"F0.wireOp",EDGE,"E23"),sQuery(id+"F0.wireOp",EDGE,"E24"),sQuery(id+"F0.wireOp",EDGE,"E25"),sQuery(id+"F0.wireOp",EDGE,"E26"),sQuery(id+"F0.wireOp",EDGE,"E27"),sQuery(id+"F0.wireOp",EDGE,"E28"),sQuery(id+"F0.wireOp",EDGE,"E29"),sQuery(id+"F0.wireOp",EDGE,"E30"),sQuery(id+"F0.wireOp",EDGE,"E31"),sQuery(id+"F0.wireOp",EDGE,"E32"),sQuery(id+"F0.wireOp",EDGE,"E33"),sQuery(id+"F0.wireOp",EDGE,"E34"),sQuery(id+"F0.wireOp",EDGE,"E35"),sQuery(id+"F0.wireOp",EDGE,"E36"),sQuery(id+"F0.wireOp",EDGE,"E37"),sQuery(id+"F0.wireOp",EDGE,"E38"),sQuery(id+"F0.wireOp",EDGE,"E39"),sQuery(id+"F0.wireOp",EDGE,"E40"),sQuery(id+"F0.wireOp",EDGE,"E41"),sQuery(id+"F0.wireOp",EDGE,"E42"),sQuery(id+"F0.wireOp",EDGE,"E43"),sQuery(id+"F0.wireOp",EDGE,"E44"),sQuery(id+"F0.wireOp",EDGE,"E45"),sQuery(id+"F0.wireOp",EDGE,"E46"),sQuery(id+"F0.wireOp",EDGE,"E47"),sQuery(id+"F0.wireOp",EDGE,"E48"),sQuery(id+"F0.wireOp",EDGE,"E49"),sQuery(id+"F0.wireOp",EDGE,"E50"),sQuery(id+"F0.wireOp",EDGE,"E51"),sQuery(id+"F0.wireOp",EDGE,"E52"),sQuery(id+"F0.wireOp",EDGE,"E53"),sQuery(id+"F0.wireOp",EDGE,"E54"),sQuery(id+"F0.wireOp",EDGE,"E55"),sQuery(id+"F0.wireOp",EDGE,"E56"),sQuery(id+"F0.wireOp",EDGE,"E57"),sQuery(id+"F0.wireOp",EDGE,"E58"),sQuery(id+"F0.wireOp",EDGE,"E59"),sQuery(id+"F0.wireOp",EDGE,"E60"),sQuery(id+"F0.wireOp",EDGE,"E61"),sQuery(id+"F0.wireOp",EDGE,"E62"),sQuery(id+"F0.wireOp",EDGE,"E63"),sQuery(id+"F0.wireOp",EDGE,"E64"),sQuery(id+"F0.wireOp",EDGE,"E65"),sQuery(id+"F0.wireOp",EDGE,"E66"),sQuery(id+"F0.wireOp",EDGE,"E67"),sQuery(id+"F0.wireOp",EDGE,"E68"),sQuery(id+"F0.wireOp",EDGE,"E69"),sQuery(id+"F0.wireOp",EDGE,"E70"),sQuery(id+"F0.wireOp",EDGE,"E71"),sQuery(id+"F0.wireOp",EDGE,"E72"),sQuery(id+"F0.wireOp",EDGE,"E73"),sQuery(id+"F0.wireOp",EDGE,"E74"),sQuery(id+"F0.wireOp",EDGE,"E75"),sQuery(id+"F0.wireOp",EDGE,"E76"),sQuery(id+"F0.wireOp",EDGE,"E77"),sQuery(id+"F0.wireOp",EDGE,"E78"),sQuery(id+"F0.wireOp",EDGE,"E79"),sQuery(id+"F0.wireOp",EDGE,"E80"),sQuery(id+"F0.wireOp",EDGE,"E81"),sQuery(id+"F0.wireOp",EDGE,"E82"),sQuery(id+"F0.wireOp",EDGE,"E83"),sQuery(id+"F0.wireOp",EDGE,"E84"),sQuery(id+"F0.wireOp",EDGE,"E85"),sQuery(id+"F0.wireOp",EDGE,"E86"),sQuery(id+"F0.wireOp",EDGE,"E87"),sQuery(id+"F0.wireOp",EDGE,"E88"),sQuery(id+"F0.wireOp",EDGE,"E89"),sQuery(id+"F0.wireOp",EDGE,"E90"),sQuery(id+"F0.wireOp",EDGE,"E91"),sQuery(id+"F0.wireOp",EDGE,"E92"),sQuery(id+"F0.wireOp",EDGE,"E93"),sQuery(id+"F0.wireOp",EDGE,"E94"),sQuery(id+"F0.wireOp",EDGE,"E95"),sQuery(id+"F0.wireOp",EDGE,"E96"),sQuery(id+"F0.wireOp",EDGE,"E97"),sQuery(id+"F0.wireOp",EDGE,"E98"),sQuery(id+"F0.wireOp",EDGE,"E99"),sQuery(id+"F0.wireOp",EDGE,"E100"),sQuery(id+"F0.wireOp",EDGE,"E101"),sQuery(id+"F0.wireOp",EDGE,"E102"),sQuery(id+"F0.wireOp",EDGE,"E103"),sQuery(id+"F0.wireOp",EDGE,"E104"),sQuery(id+"F0.wireOp",EDGE,"E105"),sQuery(id+"F0.wireOp",EDGE,"E106"),sQuery(id+"F0.wireOp",EDGE,"E107"),sQuery(id+"F0.wireOp",EDGE,"E108"),sQuery(id+"F0.wireOp",EDGE,"E109"),sQuery(id+"F0.wireOp",EDGE,"E110"),sQuery(id+"F0.wireOp",EDGE,"E111"),sQuery(id+"F0.wireOp",EDGE,"E112"),sQuery(id+"F0.wireOp",EDGE,"E113"),sQuery(id+"F0.wireOp",EDGE,"E114"),sQuery(id+"F0.wireOp",EDGE,"E115"),sQuery(id+"F0.wireOp",EDGE,"E116"),sQuery(id+"F0.wireOp",EDGE,"E117"),sQuery(id+"F0.wireOp",EDGE,"E118"),sQuery(id+"F0.wireOp",EDGE,"E119"),sQuery(id+"F0.wireOp",EDGE,"E120"),sQuery(id+"F0.wireOp",EDGE,"E121"),sQuery(id+"F0.wireOp",EDGE,"E122"),sQuery(id+"F0.wireOp",EDGE,"E123"),sQuery(id+"F0.wireOp",EDGE,"E124"),sQuery(id+"F0.wireOp",EDGE,"E125"),sQuery(id+"F0.wireOp",EDGE,"E126"),sQuery(id+"F0.wireOp",EDGE,"E127"),sQuery(id+"F0.wireOp",EDGE,"E128"),sQuery(id+"F0.wireOp",EDGE,"E129"),sQuery(id+"F0.wireOp",EDGE,"E130"),sQuery(id+"F0.wireOp",EDGE,"E131"),sQuery(id+"F0.wireOp",EDGE,"E132"),sQuery(id+"F0.wireOp",EDGE,"E133"),sQuery(id+"F0.wireOp",EDGE,"E134"),sQuery(id+"F0.wireOp",EDGE,"E135"),sQuery(id+"F0.wireOp",EDGE,"E136"),sQuery(id+"F0.wireOp",EDGE,"E137"),sQuery(id+"F0.wireOp",EDGE,"E138"),sQuery(id+"F0.wireOp",EDGE,"E139"),sQuery(id+"F0.wireOp",EDGE,"E140"),sQuery(id+"F0.wireOp",EDGE,"E141"),sQuery(id+"F0.wireOp",EDGE,"E142"),sQuery(id+"F0.wireOp",EDGE,"E143"),sQuery(id+"F0.wireOp",EDGE,"E144"),sQuery(id+"F0.wireOp",EDGE,"E145"),sQuery(id+"F0.wireOp",EDGE,"E146"),sQuery(id+"F0.wireOp",EDGE,"E147"),sQuery(id+"F0.wireOp",EDGE,"E148"),sQuery(id+"F0.wireOp",EDGE,"E149"),sQuery(id+"F0.wireOp",EDGE,"E150"),sQuery(id+"F0.wireOp",EDGE,"E151"),sQuery(id+"F0.wireOp",EDGE,"E152"),sQuery(id+"F0.wireOp",EDGE,"E153"),sQuery(id+"F0.wireOp",EDGE,"E154"),sQuery(id+"F0.wireOp",EDGE,"E155"),sQuery(id+"F0.wireOp",EDGE,"E156"),sQuery(id+"F0.wireOp",EDGE,"E157"),sQuery(id+"F0.wireOp",EDGE,"E158"),sQuery(id+"F0.wireOp",EDGE,"E159"),sQuery(id+"F0.wireOp",EDGE,"E160"),sQuery(id+"F0.wireOp",EDGE,"E161"),sQuery(id+"F0.wireOp",EDGE,"E162"),sQuery(id+"F0.wireOp",EDGE,"E163"),sQuery(id+"F0.wireOp",EDGE,"E164"),sQuery(id+"F0.wireOp",EDGE,"E165"),sQuery(id+"F0.wireOp",EDGE,"E166"),sQuery(id+"F0.wireOp",EDGE,"E167")])],"isStart":false})});
            var sketch = newSketch(context, id + "F7", { "sketchPlane" : qUnion([Q0])});
            skCircle(sketch, "E170", {"center": v(0, 0) * mm, "radius": 7 * mm});
            skSolve(sketch);
        }
        {
            var Q0;
            Q0 = qSketchRegion(id + "F7", true);
            extrude(context, id + "F8", {"entities" : qUnion([Q0]), "operationType" : NewBodyOperationType.ADD, "depth" : 2 * mm, "offsetDistance" : 25 * mm});
        }
        {
            var Q0;
            Q0=makeQuery(id+"F8.boolean.opBoolean","SPLIT",FACE,{"disambiguationData":[TD([makeQuery(id+"F5.boolean.opBoolean","COPY",FACE,{"derivedFrom":makeQuery(id+"F5.opExtrude","SWEPT_FACE",FACE,{"disambiguationData":[OSD([sQuery(id+"F4.wireOp",EDGE,"E169")])]})})])],"derivedFrom":makeQuery(id+"F8.opExtrude","CAP_FACE",FACE,{"disambiguationData":[OSD([sQuery(id+"F7.wireOp",EDGE,"E170")])],"isStart":true})});
            extrude(context, id + "F9", {"entities" : qUnion([Q0]), "operationType" : NewBodyOperationType.REMOVE, "oppositeDirection" : true, "depth" : 25 * mm, "offsetDistance" : 25 * mm});
        }
        {
            var Q0;
            Q0=makeQuery(id+"F8.opExtrude","CAP_FACE",FACE,{"disambiguationData":[OSD([sQuery(id+"F7.wireOp",EDGE,"E170")])],"isStart":false});
            var sketch = newSketch(context, id + "F10", { "sketchPlane" : qUnion([Q0])});
            skCircle(sketch, "E171", {"center": v(0, 0) * mm, "radius": 2.5 * mm});
            skCircle(sketch, "E172", {"center": v(0, 0) * mm, "radius": 10 * mm});
            skSolve(sketch);
        }
        {
            var Q0;
            Q0 = qSketchRegion(id + "F10", true);
            extrude(context, id + "F11", {"entities" : qUnion([Q0]), "operationType" : NewBodyOperationType.ADD, "oppositeDirection" : true, "depth" : 2 * mm, "offsetDistance" : 25 * mm});
        }
        {
            var Q0;
            Q0=makeQuery(id+"F11.boolean.opBoolean","MERGE",FACE,{"derivedFrom":[makeQuery(id+"F8.opExtrude","CAP_FACE",FACE,{"disambiguationData":[OSD([sQuery(id+"F7.wireOp",EDGE,"E170")])],"isStart":false}),makeQuery(id+"F11.opExtrude","CAP_FACE",FACE,{"disambiguationData":[OSD([sQuery(id+"F10.wireOp",EDGE,"E171"),sQuery(id+"F10.wireOp",EDGE,"E172")])],"isStart":true})]});
            extrude(context, id + "F12", {"entities" : qUnion([Q0]), "operationType" : NewBodyOperationType.ADD, "depth" : 1.6 * mm, "offsetDistance" : 25 * mm});
        }
        {
            var Q0;
            Q0=makeQuery(id+"F12.opExtrude","CAP_FACE",FACE,{"disambiguationData":[OSD([sQuery(id+"F7.wireOp",EDGE,"E170"),sQuery(id+"F10.wireOp",EDGE,"E171"),sQuery(id+"F10.wireOp",EDGE,"E172")])],"isStart":false});
            var sketch = newSketch(context, id + "F13", { "sketchPlane" : qUnion([Q0])});
            skCircle(sketch, "E173", {"center": v(0, 0) * mm, "radius": 2.5 * mm});
            skCircle(sketch, "E174", {"center": v(0, 0) * mm, "radius": 27 * mm});
            skSolve(sketch);
        }
        {
            var Q0;
            Q0 = qSketchRegion(id + "F13", true);
            extrude(context, id + "F14", {"entities" : qUnion([Q0]), "operationType" : NewBodyOperationType.ADD, "oppositeDirection" : true, "depth" : 1.5 * mm, "offsetDistance" : 25 * mm});
        }
        {
            var Q0;
            Q0=makeQuery(id+"F14.opExtrude","CAP_FACE",FACE,{"disambiguationData":[OSD([sQuery(id+"F13.wireOp",EDGE,"E173"),sQuery(id+"F13.wireOp",EDGE,"E174")])],"isStart":false});
            var sketch = newSketch(context, id + "F15", { "sketchPlane" : qUnion([Q0])});
            skCircle(sketch, "E175", {"center": v(0, 0) * mm, "radius": 27 * mm});
            skCircle(sketch, "E176", {"center": v(0, 0) * mm, "radius": 26 * mm});
            skSolve(sketch);
        }
        {
            var Q0;
            Q0 = qSketchRegion(id + "F15", true);
            extrude(context, id + "F16", {"entities" : qUnion([Q0]), "operationType" : NewBodyOperationType.ADD, "depth" : 8 * mm, "offsetDistance" : 25 * mm});
        }
        {
            var Q0;
            Q0=makeQuery(id+"F14.opExtrude","CAP_FACE",FACE,{"disambiguationData":[OSD([sQuery(id+"F13.wireOp",EDGE,"E173"),sQuery(id+"F13.wireOp",EDGE,"E174")])],"isStart":false});
            var sketch = newSketch(context, id + "F17", { "sketchPlane" : qUnion([Q0])});
            skCircle(sketch, "E177", {"center": v(0, 0) * mm, "radius": 25 * mm});
            skCircle(sketch, "E178", {"center": v(0, 0) * mm, "radius": 26 * mm});
            skSolve(sketch);
        }
        {
            var Q0;
            Q0 = qSketchRegion(id + "F17", true);
            extrude(context, id + "F18", {"entities" : qUnion([Q0]), "operationType" : NewBodyOperationType.ADD, "depth" : 1 * mm, "offsetDistance" : 25 * mm});
        }
        {
            var Q0;
            Q0=makeQuery(id+"F14.boolean.opBoolean","MERGE",FACE,{"derivedFrom":[makeQuery(id+"F12.opExtrude","CAP_FACE",FACE,{"disambiguationData":[OSD([sQuery(id+"F7.wireOp",EDGE,"E170"),sQuery(id+"F10.wireOp",EDGE,"E171"),sQuery(id+"F10.wireOp",EDGE,"E172")])],"isStart":false}),makeQuery(id+"F14.opExtrude","CAP_FACE",FACE,{"disambiguationData":[OSD([sQuery(id+"F13.wireOp",EDGE,"E173"),sQuery(id+"F13.wireOp",EDGE,"E174")])],"isStart":true})]});
            var sketch = newSketch(context, id + "F19", { "sketchPlane" : qUnion([Q0])});
            skCircle(sketch, "E179", {"center": v(0, 0) * mm, "radius": 3 * mm});
            skSolve(sketch);
        }
        {
            var Q0;
            Q0 = qSketchRegion(id + "F19", true);
            extrude(context, id + "F20", {"entities" : qUnion([Q0]), "operationType" : NewBodyOperationType.REMOVE, "oppositeDirection" : true, "depth" : 5 * mm, "offsetDistance" : 25 * mm});
        }
        {
            var Q0;
            {var subQ0=sQuery(id+"F7.wireOp",EDGE,"E170");var subQ1=makeQuery(id+"F8.opExtrude","SWEPT_FACE",FACE,{"disambiguationData":[OSD([subQ0])]});var subQ2=makeQuery(id+"F8.opExtrude","CAP_FACE",FACE,{"disambiguationData":[OSD([subQ0])],"isStart":true});Q0=makeQuery(id+"F11.boolean.opBoolean","MERGE",FACE,{"derivedFrom":[makeQuery(id+"F8.boolean.opBoolean","SPLIT",FACE,{"disambiguationData":[TD([makeQuery(id+"F1.opExtrude","SWEPT_FACE",FACE,{"disambiguationData":[OSD([sQuery(id+"F0.wireOp",EDGE,"E0")])]}),makeQuery(id+"F1.opExtrude","SWEPT_FACE",FACE,{"disambiguationData":[OSD([sQuery(id+"F0.wireOp",EDGE,"E1")])]}),makeQuery(id+"F1.opExtrude","SWEPT_FACE",FACE,{"disambiguationData":[OSD([sQuery(id+"F0.wireOp",EDGE,"E2")])]}),makeQuery(id+"F1.opExtrude","SWEPT_FACE",FACE,{"disambiguationData":[OSD([sQuery(id+"F0.wireOp",EDGE,"E3")])]}),makeQuery(id+"F1.opExtrude","SWEPT_FACE",FACE,{"disambiguationData":[OSD([sQuery(id+"F0.wireOp",EDGE,"E4")])]}),makeQuery(id+"F1.opExtrude","SWEPT_FACE",FACE,{"disambiguationData":[OSD([sQuery(id+"F0.wireOp",EDGE,"E5")])]}),makeQuery(id+"F1.opExtrude","SWEPT_FACE",FACE,{"disambiguationData":[OSD([sQuery(id+"F0.wireOp",EDGE,"E6")])]}),makeQuery(id+"F1.opExtrude","SWEPT_FACE",FACE,{"disambiguationData":[OSD([sQuery(id+"F0.wireOp",EDGE,"E161")])]}),makeQuery(id+"F1.opExtrude","SWEPT_FACE",FACE,{"disambiguationData":[OSD([sQuery(id+"F0.wireOp",EDGE,"E162")])]}),makeQuery(id+"F1.opExtrude","SWEPT_FACE",FACE,{"disambiguationData":[OSD([sQuery(id+"F0.wireOp",EDGE,"E163")])]}),makeQuery(id+"F1.opExtrude","SWEPT_FACE",FACE,{"disambiguationData":[OSD([sQuery(id+"F0.wireOp",EDGE,"E164")])]}),makeQuery(id+"F1.opExtrude","SWEPT_FACE",FACE,{"disambiguationData":[OSD([sQuery(id+"F0.wireOp",EDGE,"E165")])]}),makeQuery(id+"F1.opExtrude","SWEPT_FACE",FACE,{"disambiguationData":[OSD([sQuery(id+"F0.wireOp",EDGE,"E166")])]}),makeQuery(id+"F1.opExtrude","SWEPT_FACE",FACE,{"disambiguationData":[OSD([sQuery(id+"F0.wireOp",EDGE,"E167")])]}),subQ1,subQ2])],"derivedFrom":subQ2}),makeQuery(id+"F8.boolean.opBoolean","SPLIT",FACE,{"disambiguationData":[TD([makeQuery(id+"F1.opExtrude","SWEPT_FACE",FACE,{"disambiguationData":[OSD([sQuery(id+"F0.wireOp",EDGE,"E7")])]}),makeQuery(id+"F1.opExtrude","SWEPT_FACE",FACE,{"disambiguationData":[OSD([sQuery(id+"F0.wireOp",EDGE,"E8")])]}),makeQuery(id+"F1.opExtrude","SWEPT_FACE",FACE,{"disambiguationData":[OSD([sQuery(id+"F0.wireOp",EDGE,"E9")])]}),makeQuery(id+"F1.opExtrude","SWEPT_FACE",FACE,{"disambiguationData":[OSD([sQuery(id+"F0.wireOp",EDGE,"E10")])]}),makeQuery(id+"F1.opExtrude","SWEPT_FACE",FACE,{"disambiguationData":[OSD([sQuery(id+"F0.wireOp",EDGE,"E11")])]}),makeQuery(id+"F1.opExtrude","SWEPT_FACE",FACE,{"disambiguationData":[OSD([sQuery(id+"F0.wireOp",EDGE,"E12")])]}),makeQuery(id+"F1.opExtrude","SWEPT_FACE",FACE,{"disambiguationData":[OSD([sQuery(id+"F0.wireOp",EDGE,"E13")])]}),makeQuery(id+"F1.opExtrude","SWEPT_FACE",FACE,{"disambiguationData":[OSD([sQuery(id+"F0.wireOp",EDGE,"E14")])]}),makeQuery(id+"F1.opExtrude","SWEPT_FACE",FACE,{"disambiguationData":[OSD([sQuery(id+"F0.wireOp",EDGE,"E15")])]}),makeQuery(id+"F1.opExtrude","SWEPT_FACE",FACE,{"disambiguationData":[OSD([sQuery(id+"F0.wireOp",EDGE,"E16")])]}),makeQuery(id+"F1.opExtrude","SWEPT_FACE",FACE,{"disambiguationData":[OSD([sQuery(id+"F0.wireOp",EDGE,"E17")])]}),makeQuery(id+"F1.opExtrude","SWEPT_FACE",FACE,{"disambiguationData":[OSD([sQuery(id+"F0.wireOp",EDGE,"E18")])]}),makeQuery(id+"F1.opExtrude","SWEPT_FACE",FACE,{"disambiguationData":[OSD([sQuery(id+"F0.wireOp",EDGE,"E19")])]}),makeQuery(id+"F1.opExtrude","SWEPT_FACE",FACE,{"disambiguationData":[OSD([sQuery(id+"F0.wireOp",EDGE,"E20")])]}),subQ1,subQ2])],"derivedFrom":subQ2}),makeQuery(id+"F8.boolean.opBoolean","SPLIT",FACE,{"disambiguationData":[TD([makeQuery(id+"F1.opExtrude","SWEPT_FACE",FACE,{"disambiguationData":[OSD([sQuery(id+"F0.wireOp",EDGE,"E21")])]}),makeQuery(id+"F1.opExtrude","SWEPT_FACE",FACE,{"disambiguationData":[OSD([sQuery(id+"F0.wireOp",EDGE,"E22")])]}),makeQuery(id+"F1.opExtrude","SWEPT_FACE",FACE,{"disambiguationData":[OSD([sQuery(id+"F0.wireOp",EDGE,"E23")])]}),makeQuery(id+"F1.opExtrude","SWEPT_FACE",FACE,{"disambiguationData":[OSD([sQuery(id+"F0.wireOp",EDGE,"E24")])]}),makeQuery(id+"F1.opExtrude","SWEPT_FACE",FACE,{"disambiguationData":[OSD([sQuery(id+"F0.wireOp",EDGE,"E25")])]}),makeQuery(id+"F1.opExtrude","SWEPT_FACE",FACE,{"disambiguationData":[OSD([sQuery(id+"F0.wireOp",EDGE,"E26")])]}),makeQuery(id+"F1.opExtrude","SWEPT_FACE",FACE,{"disambiguationData":[OSD([sQuery(id+"F0.wireOp",EDGE,"E27")])]}),makeQuery(id+"F1.opExtrude","SWEPT_FACE",FACE,{"disambiguationData":[OSD([sQuery(id+"F0.wireOp",EDGE,"E28")])]}),makeQuery(id+"F1.opExtrude","SWEPT_FACE",FACE,{"disambiguationData":[OSD([sQuery(id+"F0.wireOp",EDGE,"E29")])]}),makeQuery(id+"F1.opExtrude","SWEPT_FACE",FACE,{"disambiguationData":[OSD([sQuery(id+"F0.wireOp",EDGE,"E30")])]}),makeQuery(id+"F1.opExtrude","SWEPT_FACE",FACE,{"disambiguationData":[OSD([sQuery(id+"F0.wireOp",EDGE,"E31")])]}),makeQuery(id+"F1.opExtrude","SWEPT_FACE",FACE,{"disambiguationData":[OSD([sQuery(id+"F0.wireOp",EDGE,"E32")])]}),makeQuery(id+"F1.opExtrude","SWEPT_FACE",FACE,{"disambiguationData":[OSD([sQuery(id+"F0.wireOp",EDGE,"E33")])]}),makeQuery(id+"F1.opExtrude","SWEPT_FACE",FACE,{"disambiguationData":[OSD([sQuery(id+"F0.wireOp",EDGE,"E34")])]}),subQ1,subQ2])],"derivedFrom":subQ2}),makeQuery(id+"F8.boolean.opBoolean","SPLIT",FACE,{"disambiguationData":[TD([makeQuery(id+"F1.opExtrude","SWEPT_FACE",FACE,{"disambiguationData":[OSD([sQuery(id+"F0.wireOp",EDGE,"E35")])]}),makeQuery(id+"F1.opExtrude","SWEPT_FACE",FACE,{"disambiguationData":[OSD([sQuery(id+"F0.wireOp",EDGE,"E36")])]}),makeQuery(id+"F1.opExtrude","SWEPT_FACE",FACE,{"disambiguationData":[OSD([sQuery(id+"F0.wireOp",EDGE,"E37")])]}),makeQuery(id+"F1.opExtrude","SWEPT_FACE",FACE,{"disambiguationData":[OSD([sQuery(id+"F0.wireOp",EDGE,"E38")])]}),makeQuery(id+"F1.opExtrude","SWEPT_FACE",FACE,{"disambiguationData":[OSD([sQuery(id+"F0.wireOp",EDGE,"E39")])]}),makeQuery(id+"F1.opExtrude","SWEPT_FACE",FACE,{"disambiguationData":[OSD([sQuery(id+"F0.wireOp",EDGE,"E40")])]}),makeQuery(id+"F1.opExtrude","SWEPT_FACE",FACE,{"disambiguationData":[OSD([sQuery(id+"F0.wireOp",EDGE,"E41")])]}),makeQuery(id+"F1.opExtrude","SWEPT_FACE",FACE,{"disambiguationData":[OSD([sQuery(id+"F0.wireOp",EDGE,"E42")])]}),makeQuery(id+"F1.opExtrude","SWEPT_FACE",FACE,{"disambiguationData":[OSD([sQuery(id+"F0.wireOp",EDGE,"E43")])]}),makeQuery(id+"F1.opExtrude","SWEPT_FACE",FACE,{"disambiguationData":[OSD([sQuery(id+"F0.wireOp",EDGE,"E44")])]}),makeQuery(id+"F1.opExtrude","SWEPT_FACE",FACE,{"disambiguationData":[OSD([sQuery(id+"F0.wireOp",EDGE,"E45")])]}),makeQuery(id+"F1.opExtrude","SWEPT_FACE",FACE,{"disambiguationData":[OSD([sQuery(id+"F0.wireOp",EDGE,"E46")])]}),makeQuery(id+"F1.opExtrude","SWEPT_FACE",FACE,{"disambiguationData":[OSD([sQuery(id+"F0.wireOp",EDGE,"E47")])]}),makeQuery(id+"F1.opExtrude","SWEPT_FACE",FACE,{"disambiguationData":[OSD([sQuery(id+"F0.wireOp",EDGE,"E48")])]}),subQ1,subQ2])],"derivedFrom":subQ2}),makeQuery(id+"F8.boolean.opBoolean","SPLIT",FACE,{"disambiguationData":[TD([makeQuery(id+"F1.opExtrude","SWEPT_FACE",FACE,{"disambiguationData":[OSD([sQuery(id+"F0.wireOp",EDGE,"E49")])]}),makeQuery(id+"F1.opExtrude","SWEPT_FACE",FACE,{"disambiguationData":[OSD([sQuery(id+"F0.wireOp",EDGE,"E50")])]}),makeQuery(id+"F1.opExtrude","SWEPT_FACE",FACE,{"disambiguationData":[OSD([sQuery(id+"F0.wireOp",EDGE,"E51")])]}),makeQuery(id+"F1.opExtrude","SWEPT_FACE",FACE,{"disambiguationData":[OSD([sQuery(id+"F0.wireOp",EDGE,"E52")])]}),makeQuery(id+"F1.opExtrude","SWEPT_FACE",FACE,{"disambiguationData":[OSD([sQuery(id+"F0.wireOp",EDGE,"E53")])]}),makeQuery(id+"F1.opExtrude","SWEPT_FACE",FACE,{"disambiguationData":[OSD([sQuery(id+"F0.wireOp",EDGE,"E54")])]}),makeQuery(id+"F1.opExtrude","SWEPT_FACE",FACE,{"disambiguationData":[OSD([sQuery(id+"F0.wireOp",EDGE,"E55")])]}),makeQuery(id+"F1.opExtrude","SWEPT_FACE",FACE,{"disambiguationData":[OSD([sQuery(id+"F0.wireOp",EDGE,"E56")])]}),makeQuery(id+"F1.opExtrude","SWEPT_FACE",FACE,{"disambiguationData":[OSD([sQuery(id+"F0.wireOp",EDGE,"E57")])]}),makeQuery(id+"F1.opExtrude","SWEPT_FACE",FACE,{"disambiguationData":[OSD([sQuery(id+"F0.wireOp",EDGE,"E58")])]}),makeQuery(id+"F1.opExtrude","SWEPT_FACE",FACE,{"disambiguationData":[OSD([sQuery(id+"F0.wireOp",EDGE,"E59")])]}),makeQuery(id+"F1.opExtrude","SWEPT_FACE",FACE,{"disambiguationData":[OSD([sQuery(id+"F0.wireOp",EDGE,"E60")])]}),makeQuery(id+"F1.opExtrude","SWEPT_FACE",FACE,{"disambiguationData":[OSD([sQuery(id+"F0.wireOp",EDGE,"E61")])]}),makeQuery(id+"F1.opExtrude","SWEPT_FACE",FACE,{"disambiguationData":[OSD([sQuery(id+"F0.wireOp",EDGE,"E62")])]}),subQ1,subQ2])],"derivedFrom":subQ2}),makeQuery(id+"F8.boolean.opBoolean","SPLIT",FACE,{"disambiguationData":[TD([makeQuery(id+"F1.opExtrude","SWEPT_FACE",FACE,{"disambiguationData":[OSD([sQuery(id+"F0.wireOp",EDGE,"E63")])]}),makeQuery(id+"F1.opExtrude","SWEPT_FACE",FACE,{"disambiguationData":[OSD([sQuery(id+"F0.wireOp",EDGE,"E64")])]}),makeQuery(id+"F1.opExtrude","SWEPT_FACE",FACE,{"disambiguationData":[OSD([sQuery(id+"F0.wireOp",EDGE,"E65")])]}),makeQuery(id+"F1.opExtrude","SWEPT_FACE",FACE,{"disambiguationData":[OSD([sQuery(id+"F0.wireOp",EDGE,"E66")])]}),makeQuery(id+"F1.opExtrude","SWEPT_FACE",FACE,{"disambiguationData":[OSD([sQuery(id+"F0.wireOp",EDGE,"E67")])]}),makeQuery(id+"F1.opExtrude","SWEPT_FACE",FACE,{"disambiguationData":[OSD([sQuery(id+"F0.wireOp",EDGE,"E68")])]}),makeQuery(id+"F1.opExtrude","SWEPT_FACE",FACE,{"disambiguationData":[OSD([sQuery(id+"F0.wireOp",EDGE,"E69")])]}),makeQuery(id+"F1.opExtrude","SWEPT_FACE",FACE,{"disambiguationData":[OSD([sQuery(id+"F0.wireOp",EDGE,"E70")])]}),makeQuery(id+"F1.opExtrude","SWEPT_FACE",FACE,{"disambiguationData":[OSD([sQuery(id+"F0.wireOp",EDGE,"E71")])]}),makeQuery(id+"F1.opExtrude","SWEPT_FACE",FACE,{"disambiguationData":[OSD([sQuery(id+"F0.wireOp",EDGE,"E72")])]}),makeQuery(id+"F1.opExtrude","SWEPT_FACE",FACE,{"disambiguationData":[OSD([sQuery(id+"F0.wireOp",EDGE,"E73")])]}),makeQuery(id+"F1.opExtrude","SWEPT_FACE",FACE,{"disambiguationData":[OSD([sQuery(id+"F0.wireOp",EDGE,"E74")])]}),makeQuery(id+"F1.opExtrude","SWEPT_FACE",FACE,{"disambiguationData":[OSD([sQuery(id+"F0.wireOp",EDGE,"E75")])]}),makeQuery(id+"F1.opExtrude","SWEPT_FACE",FACE,{"disambiguationData":[OSD([sQuery(id+"F0.wireOp",EDGE,"E76")])]}),subQ1,subQ2])],"derivedFrom":subQ2}),makeQuery(id+"F8.boolean.opBoolean","SPLIT",FACE,{"disambiguationData":[TD([makeQuery(id+"F1.opExtrude","SWEPT_FACE",FACE,{"disambiguationData":[OSD([sQuery(id+"F0.wireOp",EDGE,"E77")])]}),makeQuery(id+"F1.opExtrude","SWEPT_FACE",FACE,{"disambiguationData":[OSD([sQuery(id+"F0.wireOp",EDGE,"E78")])]}),makeQuery(id+"F1.opExtrude","SWEPT_FACE",FACE,{"disambiguationData":[OSD([sQuery(id+"F0.wireOp",EDGE,"E79")])]}),makeQuery(id+"F1.opExtrude","SWEPT_FACE",FACE,{"disambiguationData":[OSD([sQuery(id+"F0.wireOp",EDGE,"E80")])]}),makeQuery(id+"F1.opExtrude","SWEPT_FACE",FACE,{"disambiguationData":[OSD([sQuery(id+"F0.wireOp",EDGE,"E81")])]}),makeQuery(id+"F1.opExtrude","SWEPT_FACE",FACE,{"disambiguationData":[OSD([sQuery(id+"F0.wireOp",EDGE,"E82")])]}),makeQuery(id+"F1.opExtrude","SWEPT_FACE",FACE,{"disambiguationData":[OSD([sQuery(id+"F0.wireOp",EDGE,"E83")])]}),makeQuery(id+"F1.opExtrude","SWEPT_FACE",FACE,{"disambiguationData":[OSD([sQuery(id+"F0.wireOp",EDGE,"E84")])]}),makeQuery(id+"F1.opExtrude","SWEPT_FACE",FACE,{"disambiguationData":[OSD([sQuery(id+"F0.wireOp",EDGE,"E85")])]}),makeQuery(id+"F1.opExtrude","SWEPT_FACE",FACE,{"disambiguationData":[OSD([sQuery(id+"F0.wireOp",EDGE,"E86")])]}),makeQuery(id+"F1.opExtrude","SWEPT_FACE",FACE,{"disambiguationData":[OSD([sQuery(id+"F0.wireOp",EDGE,"E87")])]}),makeQuery(id+"F1.opExtrude","SWEPT_FACE",FACE,{"disambiguationData":[OSD([sQuery(id+"F0.wireOp",EDGE,"E88")])]}),makeQuery(id+"F1.opExtrude","SWEPT_FACE",FACE,{"disambiguationData":[OSD([sQuery(id+"F0.wireOp",EDGE,"E89")])]}),makeQuery(id+"F1.opExtrude","SWEPT_FACE",FACE,{"disambiguationData":[OSD([sQuery(id+"F0.wireOp",EDGE,"E90")])]}),subQ1,subQ2])],"derivedFrom":subQ2}),makeQuery(id+"F8.boolean.opBoolean","SPLIT",FACE,{"disambiguationData":[TD([makeQuery(id+"F1.opExtrude","SWEPT_FACE",FACE,{"disambiguationData":[OSD([sQuery(id+"F0.wireOp",EDGE,"E91")])]}),makeQuery(id+"F1.opExtrude","SWEPT_FACE",FACE,{"disambiguationData":[OSD([sQuery(id+"F0.wireOp",EDGE,"E92")])]}),makeQuery(id+"F1.opExtrude","SWEPT_FACE",FACE,{"disambiguationData":[OSD([sQuery(id+"F0.wireOp",EDGE,"E93")])]}),makeQuery(id+"F1.opExtrude","SWEPT_FACE",FACE,{"disambiguationData":[OSD([sQuery(id+"F0.wireOp",EDGE,"E94")])]}),makeQuery(id+"F1.opExtrude","SWEPT_FACE",FACE,{"disambiguationData":[OSD([sQuery(id+"F0.wireOp",EDGE,"E95")])]}),makeQuery(id+"F1.opExtrude","SWEPT_FACE",FACE,{"disambiguationData":[OSD([sQuery(id+"F0.wireOp",EDGE,"E96")])]}),makeQuery(id+"F1.opExtrude","SWEPT_FACE",FACE,{"disambiguationData":[OSD([sQuery(id+"F0.wireOp",EDGE,"E97")])]}),makeQuery(id+"F1.opExtrude","SWEPT_FACE",FACE,{"disambiguationData":[OSD([sQuery(id+"F0.wireOp",EDGE,"E98")])]}),makeQuery(id+"F1.opExtrude","SWEPT_FACE",FACE,{"disambiguationData":[OSD([sQuery(id+"F0.wireOp",EDGE,"E99")])]}),makeQuery(id+"F1.opExtrude","SWEPT_FACE",FACE,{"disambiguationData":[OSD([sQuery(id+"F0.wireOp",EDGE,"E100")])]}),makeQuery(id+"F1.opExtrude","SWEPT_FACE",FACE,{"disambiguationData":[OSD([sQuery(id+"F0.wireOp",EDGE,"E101")])]}),makeQuery(id+"F1.opExtrude","SWEPT_FACE",FACE,{"disambiguationData":[OSD([sQuery(id+"F0.wireOp",EDGE,"E102")])]}),makeQuery(id+"F1.opExtrude","SWEPT_FACE",FACE,{"disambiguationData":[OSD([sQuery(id+"F0.wireOp",EDGE,"E103")])]}),makeQuery(id+"F1.opExtrude","SWEPT_FACE",FACE,{"disambiguationData":[OSD([sQuery(id+"F0.wireOp",EDGE,"E104")])]}),subQ1,subQ2])],"derivedFrom":subQ2}),makeQuery(id+"F8.boolean.opBoolean","SPLIT",FACE,{"disambiguationData":[TD([makeQuery(id+"F1.opExtrude","SWEPT_FACE",FACE,{"disambiguationData":[OSD([sQuery(id+"F0.wireOp",EDGE,"E105")])]}),makeQuery(id+"F1.opExtrude","SWEPT_FACE",FACE,{"disambiguationData":[OSD([sQuery(id+"F0.wireOp",EDGE,"E106")])]}),makeQuery(id+"F1.opExtrude","SWEPT_FACE",FACE,{"disambiguationData":[OSD([sQuery(id+"F0.wireOp",EDGE,"E107")])]}),makeQuery(id+"F1.opExtrude","SWEPT_FACE",FACE,{"disambiguationData":[OSD([sQuery(id+"F0.wireOp",EDGE,"E108")])]}),makeQuery(id+"F1.opExtrude","SWEPT_FACE",FACE,{"disambiguationData":[OSD([sQuery(id+"F0.wireOp",EDGE,"E109")])]}),makeQuery(id+"F1.opExtrude","SWEPT_FACE",FACE,{"disambiguationData":[OSD([sQuery(id+"F0.wireOp",EDGE,"E110")])]}),makeQuery(id+"F1.opExtrude","SWEPT_FACE",FACE,{"disambiguationData":[OSD([sQuery(id+"F0.wireOp",EDGE,"E111")])]}),makeQuery(id+"F1.opExtrude","SWEPT_FACE",FACE,{"disambiguationData":[OSD([sQuery(id+"F0.wireOp",EDGE,"E112")])]}),makeQuery(id+"F1.opExtrude","SWEPT_FACE",FACE,{"disambiguationData":[OSD([sQuery(id+"F0.wireOp",EDGE,"E113")])]}),makeQuery(id+"F1.opExtrude","SWEPT_FACE",FACE,{"disambiguationData":[OSD([sQuery(id+"F0.wireOp",EDGE,"E114")])]}),makeQuery(id+"F1.opExtrude","SWEPT_FACE",FACE,{"disambiguationData":[OSD([sQuery(id+"F0.wireOp",EDGE,"E115")])]}),makeQuery(id+"F1.opExtrude","SWEPT_FACE",FACE,{"disambiguationData":[OSD([sQuery(id+"F0.wireOp",EDGE,"E116")])]}),makeQuery(id+"F1.opExtrude","SWEPT_FACE",FACE,{"disambiguationData":[OSD([sQuery(id+"F0.wireOp",EDGE,"E117")])]}),makeQuery(id+"F1.opExtrude","SWEPT_FACE",FACE,{"disambiguationData":[OSD([sQuery(id+"F0.wireOp",EDGE,"E118")])]}),subQ1,subQ2])],"derivedFrom":subQ2}),makeQuery(id+"F8.boolean.opBoolean","SPLIT",FACE,{"disambiguationData":[TD([makeQuery(id+"F1.opExtrude","SWEPT_FACE",FACE,{"disambiguationData":[OSD([sQuery(id+"F0.wireOp",EDGE,"E119")])]}),makeQuery(id+"F1.opExtrude","SWEPT_FACE",FACE,{"disambiguationData":[OSD([sQuery(id+"F0.wireOp",EDGE,"E120")])]}),makeQuery(id+"F1.opExtrude","SWEPT_FACE",FACE,{"disambiguationData":[OSD([sQuery(id+"F0.wireOp",EDGE,"E121")])]}),makeQuery(id+"F1.opExtrude","SWEPT_FACE",FACE,{"disambiguationData":[OSD([sQuery(id+"F0.wireOp",EDGE,"E122")])]}),makeQuery(id+"F1.opExtrude","SWEPT_FACE",FACE,{"disambiguationData":[OSD([sQuery(id+"F0.wireOp",EDGE,"E123")])]}),makeQuery(id+"F1.opExtrude","SWEPT_FACE",FACE,{"disambiguationData":[OSD([sQuery(id+"F0.wireOp",EDGE,"E124")])]}),makeQuery(id+"F1.opExtrude","SWEPT_FACE",FACE,{"disambiguationData":[OSD([sQuery(id+"F0.wireOp",EDGE,"E125")])]}),makeQuery(id+"F1.opExtrude","SWEPT_FACE",FACE,{"disambiguationData":[OSD([sQuery(id+"F0.wireOp",EDGE,"E126")])]}),makeQuery(id+"F1.opExtrude","SWEPT_FACE",FACE,{"disambiguationData":[OSD([sQuery(id+"F0.wireOp",EDGE,"E127")])]}),makeQuery(id+"F1.opExtrude","SWEPT_FACE",FACE,{"disambiguationData":[OSD([sQuery(id+"F0.wireOp",EDGE,"E128")])]}),makeQuery(id+"F1.opExtrude","SWEPT_FACE",FACE,{"disambiguationData":[OSD([sQuery(id+"F0.wireOp",EDGE,"E129")])]}),makeQuery(id+"F1.opExtrude","SWEPT_FACE",FACE,{"disambiguationData":[OSD([sQuery(id+"F0.wireOp",EDGE,"E130")])]}),makeQuery(id+"F1.opExtrude","SWEPT_FACE",FACE,{"disambiguationData":[OSD([sQuery(id+"F0.wireOp",EDGE,"E131")])]}),makeQuery(id+"F1.opExtrude","SWEPT_FACE",FACE,{"disambiguationData":[OSD([sQuery(id+"F0.wireOp",EDGE,"E132")])]}),subQ1,subQ2])],"derivedFrom":subQ2}),makeQuery(id+"F8.boolean.opBoolean","SPLIT",FACE,{"disambiguationData":[TD([makeQuery(id+"F1.opExtrude","SWEPT_FACE",FACE,{"disambiguationData":[OSD([sQuery(id+"F0.wireOp",EDGE,"E133")])]}),makeQuery(id+"F1.opExtrude","SWEPT_FACE",FACE,{"disambiguationData":[OSD([sQuery(id+"F0.wireOp",EDGE,"E134")])]}),makeQuery(id+"F1.opExtrude","SWEPT_FACE",FACE,{"disambiguationData":[OSD([sQuery(id+"F0.wireOp",EDGE,"E135")])]}),makeQuery(id+"F1.opExtrude","SWEPT_FACE",FACE,{"disambiguationData":[OSD([sQuery(id+"F0.wireOp",EDGE,"E136")])]}),makeQuery(id+"F1.opExtrude","SWEPT_FACE",FACE,{"disambiguationData":[OSD([sQuery(id+"F0.wireOp",EDGE,"E137")])]}),makeQuery(id+"F1.opExtrude","SWEPT_FACE",FACE,{"disambiguationData":[OSD([sQuery(id+"F0.wireOp",EDGE,"E138")])]}),makeQuery(id+"F1.opExtrude","SWEPT_FACE",FACE,{"disambiguationData":[OSD([sQuery(id+"F0.wireOp",EDGE,"E139")])]}),makeQuery(id+"F1.opExtrude","SWEPT_FACE",FACE,{"disambiguationData":[OSD([sQuery(id+"F0.wireOp",EDGE,"E140")])]}),makeQuery(id+"F1.opExtrude","SWEPT_FACE",FACE,{"disambiguationData":[OSD([sQuery(id+"F0.wireOp",EDGE,"E141")])]}),makeQuery(id+"F1.opExtrude","SWEPT_FACE",FACE,{"disambiguationData":[OSD([sQuery(id+"F0.wireOp",EDGE,"E142")])]}),makeQuery(id+"F1.opExtrude","SWEPT_FACE",FACE,{"disambiguationData":[OSD([sQuery(id+"F0.wireOp",EDGE,"E143")])]}),makeQuery(id+"F1.opExtrude","SWEPT_FACE",FACE,{"disambiguationData":[OSD([sQuery(id+"F0.wireOp",EDGE,"E144")])]}),makeQuery(id+"F1.opExtrude","SWEPT_FACE",FACE,{"disambiguationData":[OSD([sQuery(id+"F0.wireOp",EDGE,"E145")])]}),makeQuery(id+"F1.opExtrude","SWEPT_FACE",FACE,{"disambiguationData":[OSD([sQuery(id+"F0.wireOp",EDGE,"E146")])]}),subQ1,subQ2])],"derivedFrom":subQ2}),makeQuery(id+"F8.boolean.opBoolean","SPLIT",FACE,{"disambiguationData":[TD([makeQuery(id+"F1.opExtrude","SWEPT_FACE",FACE,{"disambiguationData":[OSD([sQuery(id+"F0.wireOp",EDGE,"E147")])]}),makeQuery(id+"F1.opExtrude","SWEPT_FACE",FACE,{"disambiguationData":[OSD([sQuery(id+"F0.wireOp",EDGE,"E148")])]}),makeQuery(id+"F1.opExtrude","SWEPT_FACE",FACE,{"disambiguationData":[OSD([sQuery(id+"F0.wireOp",EDGE,"E149")])]}),makeQuery(id+"F1.opExtrude","SWEPT_FACE",FACE,{"disambiguationData":[OSD([sQuery(id+"F0.wireOp",EDGE,"E150")])]}),makeQuery(id+"F1.opExtrude","SWEPT_FACE",FACE,{"disambiguationData":[OSD([sQuery(id+"F0.wireOp",EDGE,"E151")])]}),makeQuery(id+"F1.opExtrude","SWEPT_FACE",FACE,{"disambiguationData":[OSD([sQuery(id+"F0.wireOp",EDGE,"E152")])]}),makeQuery(id+"F1.opExtrude","SWEPT_FACE",FACE,{"disambiguationData":[OSD([sQuery(id+"F0.wireOp",EDGE,"E153")])]}),makeQuery(id+"F1.opExtrude","SWEPT_FACE",FACE,{"disambiguationData":[OSD([sQuery(id+"F0.wireOp",EDGE,"E154")])]}),makeQuery(id+"F1.opExtrude","SWEPT_FACE",FACE,{"disambiguationData":[OSD([sQuery(id+"F0.wireOp",EDGE,"E155")])]}),makeQuery(id+"F1.opExtrude","SWEPT_FACE",FACE,{"disambiguationData":[OSD([sQuery(id+"F0.wireOp",EDGE,"E156")])]}),makeQuery(id+"F1.opExtrude","SWEPT_FACE",FACE,{"disambiguationData":[OSD([sQuery(id+"F0.wireOp",EDGE,"E157")])]}),makeQuery(id+"F1.opExtrude","SWEPT_FACE",FACE,{"disambiguationData":[OSD([sQuery(id+"F0.wireOp",EDGE,"E158")])]}),makeQuery(id+"F1.opExtrude","SWEPT_FACE",FACE,{"disambiguationData":[OSD([sQuery(id+"F0.wireOp",EDGE,"E159")])]}),makeQuery(id+"F1.opExtrude","SWEPT_FACE",FACE,{"disambiguationData":[OSD([sQuery(id+"F0.wireOp",EDGE,"E160")])]}),subQ1,subQ2])],"derivedFrom":subQ2}),makeQuery(id+"F11.opExtrude","CAP_FACE",FACE,{"disambiguationData":[OSD([sQuery(id+"F10.wireOp",EDGE,"E171"),sQuery(id+"F10.wireOp",EDGE,"E172")])],"isStart":false})]});}
            var sketch = newSketch(context, id + "F21", { "sketchPlane" : qUnion([Q0])});
            skCircle(sketch, "E180", {"center": v(0, 0) * mm, "radius": 9.5 * mm});
            skCircle(sketch, "E181", {"center": v(0, 0) * mm, "radius": 10 * mm});
            skSolve(sketch);
        }
        {
            var Q0;
            Q0 = qSketchRegion(id + "F21", true);
            extrude(context, id + "F22", {"entities" : qUnion([Q0]), "operationType" : NewBodyOperationType.REMOVE, "oppositeDirection" : true, "depth" : 2.1 * mm, "offsetDistance" : 25 * mm});
        }
        {
            var Q0;
            Q0=makeQuery(id+"F14.boolean.opBoolean","MERGE",FACE,{"derivedFrom":[makeQuery(id+"F12.opExtrude","CAP_FACE",FACE,{"disambiguationData":[OSD([sQuery(id+"F7.wireOp",EDGE,"E170"),sQuery(id+"F10.wireOp",EDGE,"E171"),sQuery(id+"F10.wireOp",EDGE,"E172")])],"isStart":false}),makeQuery(id+"F14.opExtrude","CAP_FACE",FACE,{"disambiguationData":[OSD([sQuery(id+"F13.wireOp",EDGE,"E173"),sQuery(id+"F13.wireOp",EDGE,"E174")])],"isStart":true})]});
            var sketch = newSketch(context, id + "F23", { "sketchPlane" : qUnion([Q0])});
            skArc(sketch, "E182", {"start": v(-25.4, -9.14) * mm, "mid": v(-14.6, -22.71) * mm, "end": v(2.24, -26.9) * mm});
            skArc(sketch, "E183", {"start": v(-5, -69.82) * mm, "mid": v(39.1, -58.06) * mm, "end": v(66.57, -21.63) * mm});
            skLineSegment(sketch, "E184", {"start": v(0, 0) * mm, "end": v(0, -70) * mm, "construction": true});
            skLineSegment(sketch, "E185", {"start": v(0, 0) * mm, "end": v(66.57, -21.63) * mm, "construction": true});
            skCircle(sketch, "E186", {"center": v(0, -70) * mm, "radius": 5 * mm, "construction": true});
            skArc(sketch, "E187", {"start": v(-4.7, -66.7) * mm, "mid": v(-2.88, -69.1) * mm, "end": v(0, -70) * mm});
            skArc(sketch, "E188", {"start": v(10.17, -48.95) * mm, "mid": v(33.37, -37.23) * mm, "end": v(47.55, -15.45) * mm});
            skLineSegment(sketch, "E189", {"start": v(47.55, -15.45) * mm, "end": v(66.57, -21.63) * mm});
            skArc(sketch, "E190", {"start": v(66.57, -21.63) * mm, "mid": v(60.15, -9.03) * mm, "end": v(47.55, -15.45) * mm});
            skLineSegment(sketch, "E191.trimOffspring", {"start": v(-4.7, -66.7) * mm, "end": v(-25.4, -9.14) * mm});
            skLineSegment(sketch, "E192", {"start": v(2.24, -26.9) * mm, "end": v(10.17, -48.95) * mm});
            skPoint(sketch, "E193.orphan", {"position": v(-10.33, 8.04) * mm});
            skSolve(sketch);
        }
        {
            var Q0;
            Q0 = qSketchRegion(id + "F23", true);
            extrude(context, id + "F24", {"entities" : qUnion([Q0]), "operationType" : NewBodyOperationType.ADD, "oppositeDirection" : true, "depth" : 9 * mm, "offsetDistance" : 25 * mm});
        }
        {
            var Q0;
            Q0=makeQuery(id+"F24.opExtrude","SWEPT_EDGE",EDGE,{"disambiguationData":[OSD([sQuery(id+"F23.wireOp",EDGE,"E188"),sQuery(id+"F23.wireOp",EDGE,"E192")])]});
            var Q1;
            Q1=makeQuery(id+"F24.opExtrude","SWEPT_EDGE",EDGE,{"disambiguationData":[OSD([sQuery(id+"F13.wireOp",EDGE,"E174"),sQuery(id+"F23.wireOp",EDGE,"E182"),sQuery(id+"F23.wireOp",EDGE,"E192")])]});
            fillet(context, id + "F25", {"entities" : qUnion([Q0, Q1]), "radius" : 5 * mm, "tangentPropagation" : true, "allowEdgeOverflow" : false});
        }
    });
